FCSTD DOCUMENT  (FreeCAD 1.1R39215 (Git))
Label: folded_glasses_assembly
License: All rights reserved
LicenseURL: http://en.wikipedia.org/wiki/All_rights_reserved
objects: App::FeaturePython×7, App::Link×4, Assembly::JointGroup×1, Assembly::AssemblyObject×1
EXTERNAL_REF file=frame.FCStd obj=Body
EXTERNAL_REF file=lens_example.FCStd obj=Body
EXTERNAL_REF file=right_temple.FCStd obj=Part
EXTERNAL_REF file=left_temple.FCStd obj=Part__Mirroring

FEATURE [App::Link] Body  label="Frame"
  LinkedObject = -> <external frame.FCStd>#Body
FEATURE [App::FeaturePython] GroundedJoint  # Assembly grounded joint (typed FeaturePython)
  ObjectToGround = -> Body
FEATURE [App::Link] Body001  label="Right lens"
  LinkPlacement = pos=(32.7,1,-2e-16) rot=(0,0,1;0rad)
  LinkedObject = -> <external lens_example.FCStd>#Body
  Placement = pos=(32.7,1,-2e-16) rot=(0,0,1;0rad)
FEATURE [App::FeaturePython] Joint  label="Right lens centering"  # Assembly joint (typed FeaturePython)
  Activated = true
  AngleMax = 0
  AngleMin = 0
  Detach1 = false
  Detach2 = false
  Distance = 0
  Distance2 = 0
  EnableAngleMax = false
  EnableAngleMin = false
  EnableLengthMax = false
  EnableLengthMin = false
  JointType = 1 (Revolute)
  LengthMax = 0
  LengthMin = 0
  Placement2 = pos=(32.7,0,0) rot=(0,0,1;0rad)
  Reference1 = -> Assembly [Body001.Sketch006.Edge1,Body001.Sketch006.Edge1]
  Reference2 = -> Assembly [Body.Sketch.Edge8,Body.Sketch.Edge8]
FEATURE [App::FeaturePython] Joint001  label="Right lens orientation"  # Assembly joint (typed FeaturePython)
  Activated = true
  AngleMax = 0
  AngleMin = 0
  Detach1 = false
  Detach2 = false
  Distance = 0
  Distance2 = 0
  EnableAngleMax = false
  EnableAngleMin = false
  EnableLengthMax = false
  EnableLengthMin = false
  JointType = 6 (Parallel)
  LengthMax = 0
  LengthMin = 0
  Placement1 = pos=(19.9369,-1.45799,-0.00317788) rot=(0.707107,0,-0.707107;3.14159rad)
  Placement2 = pos=(-56.2,-6e-16,-2.525) rot=(0.57735,-0.57735,0.57735;4.18879rad)
  Reference1 = -> Assembly [Body001.Face3,Body001.Face3]
  Reference2 = -> Assembly [Body.Face11,Body.Face11]
FEATURE [App::Link] Right_temple  label="Right temple"
  LinkPlacement = pos=(56.2,-2.5,1.187e-13) rot=(0.224951,0,0.97437;4.59055rad)
  LinkedObject = -> <external right_temple.FCStd>#Part
  Placement = pos=(56.2,-2.5,1.187e-13) rot=(0.224951,0,0.97437;4.59055rad)
FEATURE [App::FeaturePython] Joint002  label="Right temple centering"  # Assembly joint (typed FeaturePython)
  Activated = true
  AngleMax = 0
  AngleMin = 0
  Detach1 = false
  Detach2 = false
  Distance = 0
  Distance2 = 0
  EnableAngleMax = false
  EnableAngleMin = false
  EnableLengthMax = false
  EnableLengthMin = false
  JointType = 1 (Revolute)
  LengthMax = 0
  LengthMin = 0
  Placement1 = pos=(-0.562378,1.2e-15,-2.43593) rot=(-0.704823,0.704823,0.080304;3.30186rad)
  Placement2 = pos=(55.6376,-2.5,-2.43593) rot=(-0.704823,0.704823,0.080304;3.30186rad)
  Reference1 = -> Assembly [Right_temple.Body.Fillet.Edge111,Right_temple.Body.Fillet.Edge111]
  Reference2 = -> Assembly [Body.SubtractivePipe001.Edge191,Body.SubtractivePipe001.Edge191]
FEATURE [App::FeaturePython] Joint003  label="Right temple opening"  # Assembly joint (typed FeaturePython)
  Activated = true
  AngleMax = 0
  AngleMin = 0
  Detach1 = false
  Detach2 = false
  Distance = 5.59
  Distance2 = 0
  EnableAngleMax = false
  EnableAngleMin = false
  EnableLengthMax = false
  EnableLengthMin = false
  JointType = 5 (Distance)
  LengthMax = 0
  LengthMin = 0
  Placement1 = pos=(56.2,1,-5) rot=(0,0,1;0rad)
  Placement2 = pos=(0.1,3.5,-5) rot=(0,0,1;0rad)
  Reference1 = -> Assembly [Body.SubtractivePipe001.Vertex16,Body.SubtractivePipe001.Vertex16]
  Reference2 = -> Assembly [Right_temple.Body.Fillet.Vertex63,Right_temple.Body.Fillet.Vertex63]
FEATURE [App::Link] Left_temple  label="Left temple"
  LinkPlacement = pos=(-56.2,-2.5,6.1e-14) rot=(-0.224951,0,0.97437;1.77201rad)
  LinkedObject = -> <external left_temple.FCStd>#Part__Mirroring
  Placement = pos=(-56.2,-2.5,6.1e-14) rot=(-0.224951,0,0.97437;1.77201rad)
FEATURE [App::FeaturePython] Joint004  label="Left temple centering"  # Assembly joint (typed FeaturePython)
  Activated = true
  AngleMax = 0
  AngleMin = 0
  Detach1 = false
  Detach2 = false
  Distance = 0
  Distance2 = 0
  EnableAngleMax = false
  EnableAngleMin = false
  EnableLengthMax = false
  EnableLengthMin = false
  JointType = 1 (Revolute)
  LengthMax = 0
  LengthMin = 0
  Placement1 = pos=(0.562378,7.1e-15,-2.43593) rot=(0.112485,-0.112485,-0.987266;1.58361rad)
  Placement2 = pos=(-55.6376,-2.5,-2.43593) rot=(0.112485,-0.112485,-0.987266;1.58361rad)
  Reference1 = -> Assembly [Left_temple.Edge111,Left_temple.Edge111]
  Reference2 = -> Assembly [Body.SubtractivePipe001.Edge123,Body.SubtractivePipe001.Edge123]
FEATURE [App::FeaturePython] Joint005  label="Left temple opening"  # Assembly joint (typed FeaturePython)
  Activated = true
  AngleMax = 0
  AngleMin = 0
  Detach1 = false
  Detach2 = false
  Distance = 5.777
  Distance2 = 0
  EnableAngleMax = false
  EnableAngleMin = false
  EnableLengthMax = false
  EnableLengthMin = false
  JointType = 5 (Distance)
  LengthMax = 0
  LengthMin = 0
  Placement1 = pos=(-56.2,1,-5) rot=(0,0,1;0rad)
  Placement2 = pos=(-0.1,3.5,-5) rot=(0,0,1;0rad)
  Reference1 = -> Assembly [Body.SubtractivePipe001.Vertex11,Body.SubtractivePipe001.Vertex11]
  Reference2 = -> Assembly [Left_temple.Vertex63,Left_temple.Vertex63]
FEATURE [Assembly::JointGroup] Joints
  Group = -> [GroundedJoint,Joint,Joint001,Joint002,Joint003,Joint004,Joint005]
FEATURE [Assembly::AssemblyObject] Assembly
  Group = -> [Joints,Body,GroundedJoint,Body001,Joint,Joint001,Right_temple,Joint002,Joint003,Left_temple,Joint004,Joint005]
  Origin = -> Origin
  Type = Assembly

RESOLVED EXTERNAL PARTS (link-assembly join: the EXTERNAL_REF files above that resolve inside this repo's crawl, each included once):
---- part frame.FCStd = doc fcstd_d1c061e1a5e6 ----
FCSTD DOCUMENT  (FreeCAD 1.1R39673 (Git))
Label: frame
License: All rights reserved
LicenseURL: http://en.wikipedia.org/wiki/All_rights_reserved
objects: Sketcher::SketchObject×15, PartDesign::Plane×6, PartDesign::Pad×3, PartDesign::Pocket×3, PartDesign::SubtractivePipe×2, PartDesign::Fillet×1, PartDesign::Line×1, PartDesign::AdditiveLoft×1, PartDesign::Mirrored×1, PartDesign::Body×1, App::Point×1
note: 70 computed .brp shape members not serialized (recipe doc carries the construction recipe); baked Part::Feature solids carry a one-line shape summary decoded from their .brp

FEATURE [Sketcher::SketchObject] Sketch  label="Lenses holder master sketch"
  ArcFitTolerance = 1e-06
  AttachmentSupport = -> [XZ_Plane]
  ExternalTypes = [0]
  FullyConstrained = true
  MakeInternals = false
  MapMode = 5
  Placement = pos=(0,0,0) rot=(1,0,0;1.5708rad)
  sketch-geometry (24):
    g0: Ellipse CenterX=-32.7 CenterY=0 CenterZ=0 NormalX=0 NormalY=0 NormalZ=1 MajorRadius=20 MinorRadius=19 AngleXU=-2.2e-15
    g1: LineSegment [constr] StartX=-12.7 StartY=0 StartZ=0 EndX=-52.7 EndY=0 EndZ=0
    g2: LineSegment [constr] StartX=-32.7 StartY=19 StartZ=0 EndX=-32.7 EndY=-19 EndZ=0
    g3: GeomPoint [constr] X=-26.455 Y=-1.37e-14 Z=0
    g4: GeomPoint [constr] X=-38.945 Y=1.39e-14 Z=0
    g5: Ellipse CenterX=32.7 CenterY=0 CenterZ=0 NormalX=0 NormalY=0 NormalZ=1 MajorRadius=20 MinorRadius=19 AngleXU=0
    g6: LineSegment [constr] StartX=52.7 StartY=0 StartZ=0 EndX=12.7 EndY=0 EndZ=0
    g7: LineSegment [constr] StartX=32.7 StartY=19 StartZ=0 EndX=32.7 EndY=-19 EndZ=0
    g8: GeomPoint [constr] X=38.945 Y=0 Z=0
    g9: GeomPoint [constr] X=26.455 Y=0 Z=0
    g10: ArcOfEllipse CenterX=-32.7 CenterY=0 CenterZ=0 NormalX=0 NormalY=0 NormalZ=1 MajorRadius=22 MinorRadius=21 AngleXU=-4.6e-15 StartAngle=0.410218 EndAngle=6.59162
    g11: LineSegment [constr] StartX=-10.7 StartY=0 StartZ=0 EndX=-54.7 EndY=0 EndZ=0
    g12: LineSegment [constr] StartX=-32.7 StartY=21 StartZ=0 EndX=-32.7 EndY=-21 EndZ=0
    g13: GeomPoint [constr] X=-26.1426 Y=-3.02e-14 Z=0
    g14: GeomPoint [constr] X=-39.2574 Y=3e-14 Z=0
    g15: ArcOfEllipse CenterX=32.7 CenterY=0 CenterZ=0 NormalX=0 NormalY=0 NormalZ=1 MajorRadius=22 MinorRadius=21 AngleXU=0 StartAngle=2.83315 EndAngle=9.01456
    g16: LineSegment [constr] StartX=54.7 StartY=0 StartZ=0 EndX=10.7 EndY=0 EndZ=0
    g17: LineSegment [constr] StartX=32.7 StartY=21 StartZ=0 EndX=32.7 EndY=-21 EndZ=0
    g18: GeomPoint [constr] X=39.2574 Y=0 Z=0
    g19: GeomPoint [constr] X=26.1426 Y=-3e-16 Z=0
    g20: LineSegment StartX=-11.7382 StartY=6.375 StartZ=0 EndX=11.7382 EndY=6.375 EndZ=0
    g21: LineSegment StartX=-12.5253 StartY=8.375 StartZ=0 EndX=12.5253 EndY=8.375 EndZ=0
    g22: Circle CenterX=-32.7 CenterY=0 CenterZ=0 NormalX=0 NormalY=0 NormalZ=1 AngleXU=0 Radius=0.5
    g23: Circle CenterX=32.7 CenterY=0 CenterZ=0 NormalX=0 NormalY=0 NormalZ=1 AngleXU=0 Radius=0.5
  constraints (33):
    c: InternalAlignment(g1-g4 -> g0) x4
    c: PointOnObject(g0,g-1)
    c: Horizontal(g1)
    c: DistanceX(g1,g1) = 40
    c: DistanceY(g2,g2) = 38
    c: InternalAlignment(g6-g9 -> g5) x4
    c: Horizontal(g6)
    c: Equal(g1,g6)
    c: Equal(g7,g2)
    c: Symmetric(g5,g0,g-2)
    c: DistanceX(g0,g5) = 65.4
    c: InternalAlignment(g11-g14 -> g10) x4
    c: Coincident(g10,g0)
    c: Horizontal(g11)
    c: InternalAlignment(g16-g19 -> g15) x4
    c: Symmetric(g0,g15,g-2)
    c: Horizontal(g16)
    c: Equal(g16,g11)
    c: Equal(g17,g12)
    c: Horizontal(g10,g15)
    c: Horizontal(g15,g10)
    c: Coincident(g20,g10)
    c: Coincident(g20,g15)
    c: Coincident(g21,g10)
    c: Coincident(g21,g15)
    c: Distance(g20,g21) = 2
    c: Distance(g-1,g20) = 6.375
    c: Coincident(g22,g0)
    c: Diameter(g22) = 1
    c: Equal(g22,g23)
    c: Symmetric(g22,g23,g-2)
    c: DistanceY(g12,g12) = 42
    c: DistanceX(g11,g11) = 44
FEATURE [PartDesign::Pad] Pad  label="Lenses holder"
  Direction = (0,-1,2e-16)
  Length = 2
  Length2 = 10
  Midplane = true
  Placement = pos=(0,0,0) rot=(1,0,0;1.5708rad)
  Profile = -> Sketch
  ReferenceAxis = -> Sketch [N_Axis]
  Suppressed = false
  Type = 0
FEATURE [Sketcher::SketchObject] Sketch001  label="Nose bridge profile #1"
  ArcFitTolerance = 1e-06
  AttachmentSupport = -> [YZ_Plane]
  ExternalTypes = [0]
  FullyConstrained = true
  MakeInternals = false
  MapMode = 5
  Placement = pos=(0,0,0) rot=(0.57735,0.57735,0.57735;2.0944rad)
  sketch-geometry (1):
    g0: LineSegment StartX=-6 StartY=0 StartZ=0 EndX=0 EndY=5.5 EndZ=0
  constraints (4):
    c: PointOnObject(g0,g-1)
    c: Distance(g0,g-1) = 5.5
    c: PointOnObject(g0,g-2)
    c: DistanceX(g0,g-1) = 6
FEATURE [Sketcher::SketchObject] Sketch002  label="Nose bridge profile #2"
  ArcFitTolerance = 1e-06
  AttachmentSupport = -> [XY_Plane]
  ExternalGeometry = -> [Sketch001]
  ExternalTypes = [0]
  FullyConstrained = true
  MakeInternals = false
  MapMode = 5
  sketch-geometry (1):
    g0: LineSegment StartX=-9.25 StartY=-6 StartZ=0 EndX=9.25 EndY=-6 EndZ=0
  constraints (3):
    c: Symmetric(g0,g0,g-2)
    c: PointOnObject(g-3,g0)
    c: DistanceX(g0,g0) = 18.5
FEATURE [PartDesign::Plane] DatumPlane  label="Nose bridge plane"
  AttachmentSupport = -> [Sketch001,Sketch002]
  Length = 134.588
  MapMode = 13
  Placement = pos=(0,-4,1.83333) rot=(1,0,0;0.741947rad)
  ResizeMode = 0
  Width = 88.7838
FEATURE [Sketcher::SketchObject] Sketch003  label="Nose bridge profile"
  ArcFitTolerance = 1e-06
  AttachmentSupport = -> [DatumPlane]
  ExternalGeometry = -> [Sketch001,Sketch002,Pad]
  ExternalTypes = [0]
  FullyConstrained = true
  MakeInternals = false
  MapMode = 5
  Placement = pos=(0,-4,1.83333) rot=(1,0,0;0.741947rad)
  sketch-geometry (21):
    g0: ArcOfEllipse CenterX=0 CenterY=-15.7131 CenterZ=0 NormalX=0 NormalY=0 NormalZ=1 MajorRadius=21.1394 MinorRadius=11.7303 AngleXU=1.5708 StartAngle=5.37473 EndAngle=7.19164
    g1: LineSegment [constr] StartX=0 StartY=5.42627 StartZ=0 EndX=0 EndY=-36.8525 EndZ=0
    g2: LineSegment [constr] StartX=-11.7303 StartY=-15.7131 StartZ=0 EndX=11.7303 EndY=-15.7131 EndZ=0
    g3: GeomPoint [constr] X=2e-15 Y=1.87305 Z=0
    g4: GeomPoint [constr] X=0 Y=-33.2993 Z=0
    g5: ArcOfEllipse CenterX=0 CenterY=-15.7131 CenterZ=0 NormalX=0 NormalY=0 NormalZ=1 MajorRadius=22.4394 MinorRadius=13.7303 AngleXU=1.5708 StartAngle=5.71213 EndAngle=6.85424
    g6: LineSegment [constr] StartX=-5e-16 StartY=6.72627 StartZ=0 EndX=5e-16 EndY=-38.1525 EndZ=0
    g7: LineSegment [constr] StartX=-13.7303 StartY=-15.7131 StartZ=0 EndX=13.7303 EndY=-15.7131 EndZ=0
    g8: GeomPoint [constr] X=2e-15 Y=2.03525 Z=0
    g9: GeomPoint [constr] X=4e-16 Y=-33.4615 Z=0
    g10: ArcOfCircle CenterX=-10.3972 CenterY=-2.21669 CenterZ=0 NormalX=0 NormalY=0 NormalZ=1 AngleXU=0 Radius=1.25 StartAngle=3.37719 EndAngle=5.87477
    g11: LineSegment StartX=-13.82 StartY=6.68686 StartZ=0 EndX=-11.6127 EndY=-2.50847 EndZ=0
    g12: GeomPoint [constr] X=-9.25 Y=-2.71314 Z=0
    g13: LineSegment StartX=11.6127 StartY=-2.50847 StartZ=0 EndX=13.82 EndY=6.68686 EndZ=0
    g14: ArcOfCircle CenterX=10.3972 CenterY=-2.21669 CenterZ=0 NormalX=0 NormalY=0 NormalZ=1 AngleXU=0 Radius=1.25 StartAngle=3.55001 EndAngle=6.04759
    g15: ArcOfCircle CenterX=-9.05082 CenterY=4.71757 CenterZ=0 NormalX=0 NormalY=0 NormalZ=1 AngleXU=0 Radius=2.25 StartAngle=3.63126 EndAngle=5.52216
    g16: LineSegment StartX=-11.0364 StartY=3.65931 StartZ=0 EndX=-12.65 EndY=6.68686 EndZ=0
    g17: ArcOfCircle CenterX=9.05082 CenterY=4.71757 CenterZ=0 NormalX=0 NormalY=0 NormalZ=1 AngleXU=0 Radius=2.25 StartAngle=3.90262 EndAngle=5.79351
    g18: LineSegment StartX=11.0364 StartY=3.65931 StartZ=0 EndX=12.65 EndY=6.68686 EndZ=0
    g19: LineSegment StartX=-13.82 StartY=6.68686 StartZ=0 EndX=-12.65 EndY=6.68686 EndZ=0
    g20: LineSegment StartX=12.65 StartY=6.68686 StartZ=0 EndX=13.82 EndY=6.68686 EndZ=0
  constraints (39):
    c: InternalAlignment(g1-g4 -> g0) x4
    c: PointOnObject(g0,g-2)
    c: Coincident(g-3,g1)
    c: PointOnObject(g-4,g0)
    c: Distance(g0,g-4) = 13
    c: InternalAlignment(g6-g9 -> g5) x4
    c: Coincident(g5,g0)
    c: DistanceY(g1,g6) = 1.3
    c: Distance(g2,g7) = 2
    c: Horizontal(g7)
    c: Tangent(g10,g11) = -1.5708
    c: Coincident(g-4,g10)
    c: PointOnObject(g12,g0)
    c: PointOnObject(g12,g10)
    c: Tangent(g0,g10,g12) = 1.5708
    c: Symmetric(g10,g13,g-2)
    c: Coincident(g-4,g14)
    c: Tangent(g13,g14) = -1.5708
    c: PointOnObject(g0,g-4)
    c: PointOnObject(g0,g-4)
    c: Radius(g10) = 1.25
    c: Horizontal(g5,g5)
    c: Coincident(g15,g5)
    c: Tangent(g16,g15) = 1.5708
    c: Symmetric(g15,g17,g-2)
    c: Tangent(g17,g5) = 1.5708
    c: Tangent(g18,g17) = -1.5708
    c: Radius(g15) = 2.25
    c: Distance(g15,g11) = 2
    c: Horizontal(g19)
    c: Distance(g19,g-4) = 9.4
    c: DistanceX(g19,g-1) = 13.82
    c: Distance(g19,g-2) = 12.65
    c: Coincident(g11,g19)
    c: Coincident(g16,g19)
    c: Symmetric(g11,g13,g-2)
    c: Symmetric(g16,g18,g-2)
    c: Coincident(g20,g18)
    c: Coincident(g20,g13)
FEATURE [PartDesign::Pad] Pad001  label="Nose bridge #1"
  BaseFeature = -> Pad
  Direction = (0,-0.675725,0.737154)
  Length = 2.8
  Length2 = 10
  Placement = pos=(0,0,0) rot=(1,0,0;1.5708rad)
  Profile = -> Sketch003
  ReferenceAxis = -> Sketch003 [N_Axis]
  Refine = true
  Suppressed = false
  Type = 0
FEATURE [Sketcher::SketchObject] Sketch010
  ArcFitTolerance = 1e-06
  AttachmentSupport = -> [Pad001]
  ExternalGeometry = -> [Pad001]
  ExternalTypes = [0]
  FullyConstrained = true
  MakeInternals = false
  MapMode = 5
  Placement = pos=(0,1.9e-15,8.375) rot=(0,0,1;3.14159rad)
  sketch-geometry (4):
    g0: LineSegment StartX=-12.5253 StartY=1 StartZ=0 EndX=-12.5253 EndY=-1 EndZ=0
    g1: LineSegment StartX=-12.5253 StartY=-1 StartZ=0 EndX=12.5253 EndY=-1 EndZ=0
    g2: LineSegment StartX=12.5253 StartY=-1 StartZ=0 EndX=12.5253 EndY=1 EndZ=0
    g3: LineSegment StartX=12.5253 StartY=1 StartZ=0 EndX=-12.5253 EndY=1 EndZ=0
  constraints (10):
    c: Coincident(g0,g1)
    c: Coincident(g1,g2)
    c: Coincident(g2,g3)
    c: Coincident(g3,g0)
    c: Vertical(g0)
    c: Vertical(g2)
    c: Horizontal(g1)
    c: Horizontal(g3)
    c: Coincident(g-3,g0)
    c: Coincident(g-4,g1)
FEATURE [PartDesign::Pocket] Pocket002  label="Nose bridge #2"
  BaseFeature = -> Pad001
  Direction = (0,0,-1)
  Length = 5
  Length2 = 5
  Placement = pos=(0,0,0) rot=(1,0,0;1.5708rad)
  Profile = -> Sketch010
  ReferenceAxis = -> Sketch010 [N_Axis]
  Refine = true
  Reversed = true
  Suppressed = false
  Type = 1
FEATURE [Sketcher::SketchObject] Sketch011
  ArcFitTolerance = 1e-06
  AttachmentSupport = -> [DatumPlane]
  ExternalGeometry = -> [Pocket002]
  ExternalTypes = [0]
  FullyConstrained = true
  MakeInternals = false
  MapMode = 5
  Placement = pos=(0,-4,1.83333) rot=(1,0,0;0.741947rad)
  sketch-geometry (5):
    g0: Ellipse CenterX=0 CenterY=-15.7131 CenterZ=0 NormalX=0 NormalY=0 NormalZ=1 MajorRadius=21.1394 MinorRadius=11.7303 AngleXU=1.5708
    g1: LineSegment [constr] StartX=0 StartY=5.42627 StartZ=0 EndX=0 EndY=-36.8525 EndZ=0
    g2: LineSegment [constr] StartX=-11.7303 StartY=-15.7131 StartZ=0 EndX=11.7303 EndY=-15.7131 EndZ=0
    g3: GeomPoint [constr] X=2e-15 Y=1.87305 Z=0
    g4: GeomPoint [constr] X=4e-16 Y=-33.2993 Z=0
  constraints (4):
    c: InternalAlignment(g1-g4 -> g0) x4
    c: Coincident(g0,g-3)
    c: Equal(g-3,g0)
    c: Vertical(g1)
FEATURE [PartDesign::Pocket] Pocket003  label="Nose bridge #3"
  BaseFeature = -> Pocket002
  Direction = (0,0.675725,-0.737154)
  Length = 5
  Length2 = 5
  Midplane = true
  Placement = pos=(0,0,0) rot=(1,0,0;1.5708rad)
  Profile = -> Sketch011
  ReferenceAxis = -> Sketch011 [N_Axis]
  Refine = true
  Suppressed = false
  Type = 1
FEATURE [PartDesign::Fillet] Fillet  label="Nose bridge #4"
  Base = -> Pocket003 [Edge55,Edge54,Edge40]
  BaseFeature = -> Pocket003
  Placement = pos=(0,0,0) rot=(1,0,0;1.5708rad)
  Radius = 0.6
  Refine = true
  SupportTransform = false
  Suppressed = false
  UseAllEdges = false
FEATURE [Sketcher::SketchObject] Sketch008  label="Hinges mid profile"
  ArcFitTolerance = 1e-06
  AttachmentSupport = -> [XY_Plane]
  ExternalGeometry = -> [Fillet]
  ExternalTypes = [0]
  FullyConstrained = true
  MakeInternals = false
  MapMode = 5
  sketch-geometry (14):
    g0: Circle CenterX=-56.2 CenterY=-2.5 CenterZ=0 NormalX=0 NormalY=0 NormalZ=1 AngleXU=0 Radius=0.55
    g1: Circle [constr] CenterX=-56.2 CenterY=-2.5 CenterZ=0 NormalX=0 NormalY=0 NormalZ=1 AngleXU=0 Radius=1.5
    g2: LineSegment [constr] StartX=-54.7 StartY=1 StartZ=0 EndX=-54.7 EndY=-1 EndZ=0
    g3: ArcOfCircle CenterX=-56.2 CenterY=-2.5 CenterZ=0 NormalX=0 NormalY=0 NormalZ=1 AngleXU=0 Radius=1.5 StartAngle=1.5708 EndAngle=6.28319
    g4: ArcOfCircle CenterX=-53.2 CenterY=-2.5 CenterZ=0 NormalX=0 NormalY=0 NormalZ=1 AngleXU=0 Radius=1.5 StartAngle=1.5708 EndAngle=3.14159
    g5: LineSegment StartX=-53.2 StartY=-1 StartZ=0 EndX=-53.2 EndY=1 EndZ=0
    g6: LineSegment StartX=-56.2 StartY=1 StartZ=0 EndX=-53.2 EndY=1 EndZ=0
    g7: Circle CenterX=56.2 CenterY=-2.5 CenterZ=0 NormalX=0 NormalY=0 NormalZ=1 AngleXU=0 Radius=0.55
    g8: ArcOfCircle CenterX=56.2 CenterY=-2.5 CenterZ=0 NormalX=0 NormalY=0 NormalZ=1 AngleXU=0 Radius=1.5 StartAngle=3.14159 EndAngle=7.85398
    g9: ArcOfCircle CenterX=53.2 CenterY=-2.5 CenterZ=0 NormalX=0 NormalY=0 NormalZ=1 AngleXU=0 Radius=1.5 StartAngle=0 EndAngle=1.5708
    g10: LineSegment StartX=53.2 StartY=-1 StartZ=0 EndX=53.2 EndY=1 EndZ=0
    g11: LineSegment StartX=56.2 StartY=1 StartZ=0 EndX=53.2 EndY=1 EndZ=0
    g12: LineSegment StartX=-56.2 StartY=-1 StartZ=0 EndX=-56.2 EndY=1 EndZ=0
    g13: LineSegment StartX=56.2 StartY=-1 StartZ=0 EndX=56.2 EndY=1 EndZ=0
  constraints (39):
    c: Coincident(g1,g0)
    c: Diameter(g1) = 3
    c: Diameter(g0) = 1.1
    c: Tangent(g1,g2)
    c: Coincident(g3,g0)
    c: Equal(g1,g3)
    c: Horizontal(g3,g0)
    c: Coincident(g4,g3)
    c: Horizontal(g4,g0)
    c: Vertical(g4,g4)
    c: Vertical(g5)
    c: Coincident(g6,g5)
    c: Horizontal(g6)
    c: PointOnObject(g2,g6)
    c: Coincident(g8,g7)
    c: Coincident(g9,g8)
    c: Coincident(g11,g10)
    c: Symmetric(g0,g7,g-2)
    c: Symmetric(g9,g4,g-2)
    c: Symmetric(g10,g5,g-2)
    c: Horizontal(g11)
    c: Equal(g8,g3)
    c: Horizontal(g9,g8)
    c: Vertical(g9,g9)
    c: Equal(g7,g0)
    c: Vertical(g0,g3)
    c: Coincident(g12,g3)
    c: Coincident(g12,g6)
    c: Vertical(g7,g8)
    c: Coincident(g13,g8)
    c: Coincident(g13,g11)
    c: Vertical(g13)
    c: Horizontal(g5,g2)
    c: Coincident(g5,g4)
    c: Coincident(g10,g9)
    c: Coincident(g2,g-3)
    c: Vertical(g2)
    c: Tangent(g1,g-3)
    c: Symmetric(g6,g3,g-1)
FEATURE [Sketcher::SketchObject] Sketch012
  ArcFitTolerance = 1e-06
  AttachmentSupport = -> [XY_Plane]
  ExternalGeometry = -> [Sketch008]
  ExternalTypes = [0]
  FullyConstrained = true
  MakeInternals = false
  MapMode = 5
  sketch-geometry (8):
    g0: LineSegment StartX=-53.2 StartY=1 StartZ=0 EndX=-56.2 EndY=1 EndZ=0
    g1: LineSegment StartX=-56.2 StartY=1 StartZ=0 EndX=-56.2 EndY=-1 EndZ=0
    g2: LineSegment StartX=-56.2 StartY=-1 StartZ=0 EndX=-53.2 EndY=-1 EndZ=0
    g3: LineSegment StartX=-53.2 StartY=-1 StartZ=0 EndX=-53.2 EndY=1 EndZ=0
    g4: LineSegment StartX=53.2 StartY=-1 StartZ=0 EndX=53.2 EndY=1 EndZ=0
    g5: LineSegment StartX=53.2 StartY=1 StartZ=0 EndX=56.2 EndY=1 EndZ=0
    g6: LineSegment StartX=56.2 StartY=1 StartZ=0 EndX=56.2 EndY=-1 EndZ=0
    g7: LineSegment StartX=56.2 StartY=-1 StartZ=0 EndX=53.2 EndY=-1 EndZ=0
  constraints (20):
    c: Coincident(g0,g1)
    c: Coincident(g1,g2)
    c: Coincident(g2,g3)
    c: Coincident(g3,g0)
    c: Horizontal(g0)
    c: Horizontal(g2)
    c: Vertical(g1)
    c: Vertical(g3)
    c: Coincident(g0,g-3)
    c: Coincident(g1,g-4)
    c: Coincident(g4,g5)
    c: Coincident(g5,g6)
    c: Coincident(g6,g7)
    c: Coincident(g7,g4)
    c: Symmetric(g6,g1,g-2)
    c: Symmetric(g4,g0,g-2)
    c: Horizontal(g5)
    c: Vertical(g6)
    c: Vertical(g4)
    c: Horizontal(g7)
FEATURE [Sketcher::SketchObject] Sketch014  label="Lens grooves paths"
  ArcFitTolerance = 1e-06
  AttachmentSupport = -> [XZ_Plane]
  ExternalGeometry = -> [Sketch]
  ExternalTypes = [0]
  FullyConstrained = true
  MakeInternals = false
  MapMode = 5
  Placement = pos=(0,0,0) rot=(1,0,0;1.5708rad)
  sketch-geometry (13):
    g0: ArcOfEllipse CenterX=32.7 CenterY=0 CenterZ=0 NormalX=0 NormalY=0 NormalZ=1 MajorRadius=20 MinorRadius=19 AngleXU=1e-16 StartAngle=0.0770976 EndAngle=6.20609
    g1: LineSegment [constr] StartX=52.7 StartY=1.2e-15 StartZ=0 EndX=12.7 EndY=-1.2e-15 EndZ=0
    g2: LineSegment [constr] StartX=32.7 StartY=19 StartZ=0 EndX=32.7 EndY=-19 EndZ=0
    g3: GeomPoint [constr] X=38.945 Y=6e-16 Z=0
    g4: GeomPoint [constr] X=26.455 Y=-4e-16 Z=0
    g5: LineSegment [constr] StartX=52.6406 StartY=1.4634 StartZ=0 EndX=52.6406 EndY=-1.4634 EndZ=0
    g6: LineSegment [constr] StartX=32.7 StartY=0 StartZ=0 EndX=53.1392 EndY=1.5 EndZ=0
    g7: LineSegment [constr] StartX=32.7 StartY=0 StartZ=0 EndX=53.1392 EndY=-1.5 EndZ=0
    g8: ArcOfEllipse CenterX=-32.7 CenterY=3.35e-14 CenterZ=0 NormalX=0 NormalY=0 NormalZ=1 MajorRadius=20 MinorRadius=19 AngleXU=-3.14159 StartAngle=0.0770976 EndAngle=6.20609
    g9: LineSegment [constr] StartX=-52.7 StartY=3.19e-14 StartZ=0 EndX=-12.7 EndY=3.51e-14 EndZ=0
    g10: LineSegment [constr] StartX=-32.7 StartY=19 StartZ=0 EndX=-32.7 EndY=-19 EndZ=0
    g11: GeomPoint [constr] X=-38.945 Y=3.27e-14 Z=0
    g12: GeomPoint [constr] X=-26.455 Y=3.4e-14 Z=0
  constraints (20):
    c: InternalAlignment(g1-g4 -> g0) x4
    c: Coincident(g0,g-3)
    c: Equal(g0,g-3)
    c: Vertical(g2)
    c: Vertical(g5)
    c: Coincident(g0,g5)
    c: Coincident(g0,g5)
    c: Coincident(g6,g0)
    c: Coincident(g7,g0)
    c: PointOnObject(g0,g6)
    c: PointOnObject(g0,g7)
    c: Equal(g6,g7)
    c: Distance(g0,g6) = 0.5
    c: DistanceY(g7,g6) = 3
    c: InternalAlignment(g9-g12 -> g8) x4
    c: Vertical(g10)
    c: Symmetric(g8,g0,g-2)
    c: Symmetric(g8,g0,g-2)
    c: Equal(g9,g1)
    c: Equal(g10,g2)
FEATURE [PartDesign::Plane] DatumPlane001  label="Right lens groove start plane"
  AttachmentSupport = -> [Sketch014]
  Length = 92.1419
  MapMode = 8
  Placement = pos=(52.6406,3e-16,1.4634) rot=(0.999177,0,0.040558;3.14159rad)
  ResizeMode = 0
  Width = 62.6119
FEATURE [PartDesign::Plane] DatumPlane002  label="Left lens groove start plane"
  AttachmentSupport = -> [Sketch014]
  Length = 92.1419
  MapMode = 8
  Placement = pos=(-52.6406,3e-16,1.4634) rot=(0.040558,0,0.999177;3.14159rad)
  ResizeMode = 0
  Width = 62.6119
FEATURE [PartDesign::Plane] DatumPlane003  label="Through-hinges vertical plane"
  AttachmentSupport = -> [XZ_Plane,Sketch008]
  Length = 60
  MapMode = 53
  Placement = pos=(0,-2.5,-6e-16) rot=(1,0,0;1.5708rad)
  ResizeMode = 0
  Width = 60
FEATURE [Sketcher::SketchObject] Sketch017  label="Hinges axes"
  ArcFitTolerance = 1e-06
  AttachmentSupport = -> [DatumPlane003]
  ExternalGeometry = -> [Sketch008]
  ExternalTypes = [0]
  FullyConstrained = true
  MakeInternals = false
  MapMode = 5
  Placement = pos=(0,-2.5,-6e-16) rot=(1,0,0;1.5708rad)
  sketch-geometry (5):
    g0: LineSegment [constr] StartX=-56.75 StartY=6e-16 StartZ=0 EndX=-56.2 EndY=6e-16 EndZ=0
    g1: LineSegment [constr] StartX=-55.65 StartY=6e-16 StartZ=0 EndX=-56.2 EndY=6e-16 EndZ=0
    g2: LineSegment StartX=-56.7624 StartY=2.43593 StartZ=0 EndX=-55.6376 EndY=-2.43593 EndZ=0
    g3: LineSegment [constr] StartX=-56.2 StartY=6e-16 StartZ=0 EndX=-56.2 EndY=2.43593 EndZ=0
    g4: LineSegment StartX=56.7624 StartY=2.43593 StartZ=0 EndX=55.6376 EndY=-2.43593 EndZ=0
  constraints (12):
    c: Coincident(g0,g-3)
    c: Coincident(g1,g-3)
    c: Coincident(g1,g0)
    c: Symmetric(g1,g0,g0)
    c: Coincident(g3,g0)
    c: Vertical(g3)
    c: Symmetric(g2,g2,g0)
    c: Horizontal(g3,g2)
    c: Angle(g3,g2) = 0.226893
    c: Distance(g2,g2) = 5
    c: Symmetric(g2,g4,g-2)
    c: Symmetric(g2,g4,g-2)
FEATURE [PartDesign::Pad] Pad003  label="End pieces"
  BaseFeature = -> Fillet
  Direction = (0,0,1)
  Length = 10
  Length2 = 10
  Midplane = true
  Placement = pos=(0,0,0) rot=(1,0,0;1.5708rad)
  Profile = -> Sketch012
  ReferenceAxis = -> Sketch012 [N_Axis]
  Refine = true
  Suppressed = false
  Type = 0
FEATURE [PartDesign::Plane] DatumPlane004  label="Left hinge top profile plane"
  AttachmentSupport = -> [Sketch017]
  Length = 63.0187
  MapMode = 7
  Placement = pos=(-56.7624,-2.5,2.43593) rot=(0.112485,-0.112485,-0.987266;1.58361rad)
  ResizeMode = 0
  Width = 97.7613
FEATURE [PartDesign::Plane] DatumPlane005  label="Left hinge bottom profile plane"
  AttachmentSupport = -> [Sketch017]
  Length = 63.0187
  MapMode = 7
  Placement = pos=(-55.6376,-2.5,-2.43593) rot=(0.112485,-0.112485,-0.987266;1.58361rad)
  ResizeMode = 0
  Width = 97.7613
FEATURE [Sketcher::SketchObject] Sketch018
  ArcFitTolerance = 1e-06
  AttachmentSupport = -> [DatumPlane004]
  ExternalGeometry = -> [Sketch008]
  ExternalTypes = [0]
  FullyConstrained = true
  MakeInternals = false
  MapMode = 5
  Placement = pos=(-56.7624,-2.5,2.43593) rot=(0.112485,-0.112485,-0.987266;1.58361rad)
  sketch-geometry (7):
    g0: LineSegment [constr] StartX=0 StartY=0 StartZ=0 EndX=0.55 EndY=0 EndZ=0
    g1: LineSegment [constr] StartX=0.55 StartY=0 StartZ=0 EndX=1.5 EndY=0 EndZ=0
    g2: Circle CenterX=0 CenterY=0 CenterZ=0 NormalX=0 NormalY=0 NormalZ=1 AngleXU=0 Radius=0.55
    g3: ArcOfCircle CenterX=0 CenterY=0 CenterZ=0 NormalX=0 NormalY=0 NormalZ=1 AngleXU=0 Radius=1.5 StartAngle=3.87634 EndAngle=7.85398
    g4: LineSegment StartX=-1.5 StartY=0 StartZ=0 EndX=-1.5 EndY=2.92311 EndZ=0
    g5: ArcOfEllipse CenterX=-2e-16 CenterY=2.92311 CenterZ=0 NormalX=0 NormalY=0 NormalZ=1 MajorRadius=1.5 MinorRadius=1.42311 AngleXU=-3.14159 StartAngle=0 EndAngle=1.5708
    g6: ArcOfCircle CenterX=0 CenterY=0 CenterZ=0 NormalX=0 NormalY=0 NormalZ=1 AngleXU=0 Radius=1.5 StartAngle=3.14159 EndAngle=3.87634
  constraints (21):
    c: Coincident(g0,g-1)
    c: PointOnObject(g0,g-4)
    c: Coincident(g1,g0)
    c: PointOnObject(g1,g-3)
    c: Horizontal(g0)
    c: Horizontal(g1)
    c: Coincident(g2,g0)
    c: PointOnObject(g0,g2)
    c: Coincident(g3,g0)
    c: PointOnObject(g4,g-1)
    c: PointOnObject(g1,g3)
    c: PointOnObject(g3,g-2)
    c: Coincident(g4,g-5)
    c: Horizontal(g4,g5)
    c: Tangent(g5,g3) = 1.5708
    c: Tangent(g5,g4) = 1.5708
    c: Distance(g3,g4) = 0.387
    c: PointOnObject(g4,g-3)
    c: Coincident(g6,g0)
    c: Coincident(g3,g6)
    c: PointOnObject(g6,g-1)
FEATURE [Sketcher::SketchObject] Sketch013
  ArcFitTolerance = 1e-06
  AttachmentSupport = -> [XZ_Plane]
  ExternalGeometry = -> [Sketch,Sketch018]
  ExternalTypes = [0]
  FullyConstrained = true
  MakeInternals = false
  MapMode = 5
  Placement = pos=(0,0,0) rot=(1,0,0;1.5708rad)
  sketch-geometry (8):
    g0: LineSegment StartX=-58.2239 StartY=-0.05 StartZ=0 EndX=-58.2239 EndY=0.05 EndZ=0
    g1: LineSegment StartX=-58.2239 StartY=0.05 StartZ=0 EndX=-52.6999 EndY=0.05 EndZ=0
    g2: LineSegment StartX=-52.6999 StartY=0.05 StartZ=0 EndX=-52.6999 EndY=-0.05 EndZ=0
    g3: LineSegment StartX=-52.6999 StartY=-0.05 StartZ=0 EndX=-58.2239 EndY=-0.05 EndZ=0
    g4: LineSegment StartX=52.6999 StartY=-0.05 StartZ=0 EndX=52.6999 EndY=0.05 EndZ=0
    g5: LineSegment StartX=52.6999 StartY=0.05 StartZ=0 EndX=58.2239 EndY=0.05 EndZ=0
    g6: LineSegment StartX=58.2239 StartY=0.05 StartZ=0 EndX=58.2239 EndY=-0.05 EndZ=0
    g7: LineSegment StartX=58.2239 StartY=-0.05 StartZ=0 EndX=52.6999 EndY=-0.05 EndZ=0
  constraints (20):
    c: Coincident(g0,g1)
    c: Coincident(g2,g3)
    c: Coincident(g3,g0)
    c: Symmetric(g0,g0,g-1)
    c: Symmetric(g2,g1,g-1)
    c: Coincident(g1,g2)
    c: Horizontal(g1)
    c: Coincident(g4,g5)
    c: Coincident(g5,g6)
    c: Coincident(g6,g7)
    c: Coincident(g7,g4)
    c: Symmetric(g0,g5,g-2)
    c: Symmetric(g2,g4,g-2)
    c: Vertical(g4)
    c: Vertical(g6)
    c: Horizontal(g7)
    c: Horizontal(g5)
    c: DistanceY(g0,g0) = 0.1
    c: PointOnObject(g1,g-3)
    c: PointOnObject(g-4,g0)
FEATURE [PartDesign::Line] DatumLine001  label="Edge of left endpiece on left hinge bottom profile plane"
  AttacherType = Attacher::AttachEngineLine
  AttachmentSupport = -> [DatumPlane005,Pad003]
  Length = 20
  MapMode = 30
  Placement = pos=(-56.2,-2.5,-2.56576) rot=(0,0.707107,0.707107;3.14159rad)
  ResizeMode = 0
FEATURE [Sketcher::SketchObject] Sketch019
  ArcFitTolerance = 1e-06
  AttachmentSupport = -> [DatumPlane005]
  ExternalGeometry = -> [Sketch008,DatumLine001]
  ExternalTypes = [0]
  FullyConstrained = true
  MakeInternals = false
  MapMode = 5
  Placement = pos=(-55.6376,-2.5,-2.43593) rot=(0.112485,-0.112485,-0.987266;1.58361rad)
  sketch-geometry (7):
    g0: LineSegment [constr] StartX=0 StartY=0 StartZ=0 EndX=0.55 EndY=0 EndZ=0
    g1: LineSegment [constr] StartX=0.55 StartY=0 StartZ=0 EndX=1.5 EndY=0 EndZ=0
    g2: Circle CenterX=0 CenterY=0 CenterZ=0 NormalX=0 NormalY=0 NormalZ=1 AngleXU=0 Radius=0.55
    g3: ArcOfCircle CenterX=0 CenterY=0 CenterZ=0 NormalX=0 NormalY=0 NormalZ=1 AngleXU=0 Radius=1.5 StartAngle=3.87623 EndAngle=7.85398
    g4: LineSegment StartX=-1.11311 StartY=-1.00547 StartZ=0 EndX=-1.5 EndY=-0.57717 EndZ=0
    g5: LineSegment StartX=-1.5 StartY=-0.57717 StartZ=0 EndX=-1.5 EndY=2.92311 EndZ=0
    g6: ArcOfEllipse CenterX=0 CenterY=2.92311 CenterZ=0 NormalX=0 NormalY=0 NormalZ=1 MajorRadius=1.5 MinorRadius=1.42311 AngleXU=9e-16 StartAngle=3.14159 EndAngle=4.71239
  constraints (20):
    c: Coincident(g0,g-4)
    c: PointOnObject(g0,g-3)
    c: Coincident(g0,g1)
    c: PointOnObject(g1,g-4)
    c: Horizontal(g0)
    c: Horizontal(g1)
    c: Coincident(g2,g0)
    c: PointOnObject(g0,g2)
    c: Coincident(g3,g0)
    c: PointOnObject(g3,g-2)
    c: PointOnObject(g1,g3)
    c: PointOnObject(g4,g-5)
    c: Coincident(g5,g4)
    c: Vertical(g5)
    c: Tangent(g4,g3) = 1.5708
    c: Tangent(g5,g6) = 1.5708
    c: Coincident(g5,g-6)
    c: Tangent(g6,g3) = 1.5708
    c: PointOnObject(g6,g-2)
    c: Distance(g3,g5) = 0.386887
FEATURE [PartDesign::AdditiveLoft] AdditiveLoft  label="Left hinge"
  BaseFeature = -> Pad003
  Closed = false
  Placement = pos=(0,0,0) rot=(1,0,0;1.5708rad)
  Profile = -> Sketch018
  Refine = true
  Ruled = false
  Sections = -> [Sketch019]
  Suppressed = false
FEATURE [PartDesign::Mirrored] Mirrored  label="Right hinge"
  BaseFeature = -> AdditiveLoft
  MirrorPlane = -> YZ_Plane
  Originals = -> [AdditiveLoft]
  Placement = pos=(0,0,0) rot=(1,0,0;1.5708rad)
  Suppressed = false
  TransformMode = 0
FEATURE [PartDesign::Pocket] Pocket  label="Frame opening slits"
  BaseFeature = -> Mirrored
  Direction = (0,1,-2e-16)
  Length = 5
  Length2 = 5
  Midplane = true
  Placement = pos=(0,0,0) rot=(1,0,0;1.5708rad)
  Profile = -> Sketch013
  ReferenceAxis = -> Sketch013 [N_Axis]
  Refine = true
  Suppressed = false
  Type = 1
FEATURE [Sketcher::SketchObject] Sketch015  label="Right lens groove profile"
  ArcFitTolerance = 1e-06
  AttachmentSupport = -> [DatumPlane001]
  ExternalGeometry = -> [Pocket]
  ExternalTypes = [0]
  FullyConstrained = true
  MakeInternals = false
  MapMode = 5
  Placement = pos=(52.6406,3e-16,1.4634) rot=(0.999177,0,0.040558;3.14159rad)
  sketch-geometry (6):
    g0: LineSegment StartX=0 StartY=0.85 StartZ=0 EndX=0.490748 EndY=0 EndZ=0
    g1: LineSegment StartX=0 StartY=-0.85 StartZ=0 EndX=0.490748 EndY=0 EndZ=0
    g2: LineSegment [constr] StartX=0 StartY=-0.85 StartZ=0 EndX=0 EndY=0.85 EndZ=0
    g3: LineSegment StartX=0 StartY=0.85 StartZ=0 EndX=-0.490748 EndY=1.7 EndZ=0
    g4: LineSegment StartX=-0.490748 StartY=1.7 StartZ=0 EndX=-0.490748 EndY=-1.7 EndZ=0
    g5: LineSegment StartX=-0.490748 StartY=-1.7 StartZ=0 EndX=0 EndY=-0.85 EndZ=0
  constraints (17):
    c: PointOnObject(g0,g-2)
    c: PointOnObject(g0,g-1)
    c: PointOnObject(g1,g-2)
    c: Coincident(g1,g0)
    c: Coincident(g2,g1)
    c: Coincident(g2,g0)
    c: Angle(g0,g1) = 2.0944
    c: Equal(g1,g0)
    c: Coincident(g0,g3)
    c: Coincident(g3,g4)
    c: Vertical(g4)
    c: Coincident(g4,g5)
    c: Coincident(g5,g1)
    c: Parallel(g5,g1)
    c: Equal(g5,g1)
    c: Parallel(g3,g0)
    c: Distance(g1,g-4) = 0.15
FEATURE [PartDesign::SubtractivePipe] SubtractivePipe  label="Right lens groove"
  AuxilleryCurvelinear = true
  AuxillerySpineTangent = false
  BaseFeature = -> Pocket
  Binormal = (0,0,0)
  Mode = 0
  Placement = pos=(0,0,0) rot=(1,0,0;1.5708rad)
  Profile = -> Sketch015
  Refine = true
  Spine = -> Sketch014 [Edge1]
  SpineTangent = false
  Suppressed = false
  Transformation = 0
  Transition = 0
FEATURE [Sketcher::SketchObject] Sketch016  label="Left lens groove profile"
  ArcFitTolerance = 1e-06
  AttachmentSupport = -> [DatumPlane002]
  ExternalGeometry = -> [SubtractivePipe,Sketch015]
  ExternalTypes = [0]
  FullyConstrained = true
  MakeInternals = false
  MapMode = 5
  Placement = pos=(-52.6406,3e-16,1.4634) rot=(0.040558,0,0.999177;3.14159rad)
  sketch-geometry (6):
    g0: LineSegment [constr] StartX=0 StartY=0.85 StartZ=0 EndX=0 EndY=-0.85 EndZ=0
    g1: LineSegment StartX=0 StartY=-0.85 StartZ=0 EndX=0.490748 EndY=0 EndZ=0
    g2: LineSegment StartX=0.490748 StartY=0 StartZ=0 EndX=0 EndY=0.85 EndZ=0
    g3: LineSegment StartX=0 StartY=0.85 StartZ=0 EndX=-0.490748 EndY=1.7 EndZ=0
    g4: LineSegment StartX=-0.490748 StartY=1.7 StartZ=0 EndX=-0.490748 EndY=-1.7 EndZ=0
    g5: LineSegment StartX=-0.490748 StartY=-1.7 StartZ=0 EndX=0 EndY=-0.85 EndZ=0
  constraints (17):
    c: PointOnObject(g0,g-2)
    c: PointOnObject(g0,g-2)
    c: Coincident(g1,g0)
    c: PointOnObject(g1,g-1)
    c: Coincident(g2,g1)
    c: Coincident(g2,g0)
    c: Equal(g2,g1)
    c: Angle(g2,g1) = 2.0944
    c: Coincident(g0,g3)
    c: Coincident(g3,g4)
    c: Vertical(g4)
    c: Coincident(g4,g5)
    c: Coincident(g5,g0)
    c: Parallel(g5,g1)
    c: Equal(g5,g1)
    c: Parallel(g3,g2)
    c: Equal(g4,g-5)
FEATURE [PartDesign::SubtractivePipe] SubtractivePipe001  label="Left lens groove"
  AuxilleryCurvelinear = true
  AuxillerySpineTangent = false
  BaseFeature = -> SubtractivePipe
  Binormal = (0,0,0)
  Mode = 0
  Placement = pos=(0,0,0) rot=(1,0,0;1.5708rad)
  Profile = -> Sketch016
  Spine = -> Sketch014 [Edge2]
  SpineTangent = false
  Suppressed = false
  Transformation = 0
  Transition = 0
FEATURE [PartDesign::Body] Body
  AllowCompound = false
  Group = -> [Sketch,Pad,Sketch001,Sketch002,DatumPlane,Sketch003,Pad001,Sketch010,Pocket002,Sketch011,Pocket003,Fillet,Sketch008,Sketch012,DatumPlane003,Sketch017,Pad003,Sketch013,DatumPlane004,DatumPlane005,DatumLine001,Sketch018,Sketch019,AdditiveLoft,Mirrored,Pocket,Sketch014,DatumPlane001,Sketch015,SubtractivePipe,DatumPlane002,Sketch016,SubtractivePipe001]
  Origin = -> Origin
  Tip = -> SubtractivePipe001
FEATURE [App::Point] Origin001  label="Origin"
  Role = Origin
---- part left_temple.FCStd = doc fcstd_11b7f681f36e ----
FCSTD DOCUMENT  (FreeCAD 1.1R39679 (Git))
Label: left_temple
License: All rights reserved
LicenseURL: http://en.wikipedia.org/wiki/All_rights_reserved
objects: Sketcher::SketchObject×14, PartDesign::Plane×7, PartDesign::Line×3, PartDesign::Pocket×3, PartDesign::AdditiveLoft×2, App::Point×2, PartDesign::Pad×1, PartDesign::SubtractiveLoft×1, PartDesign::AdditivePipe×1, PartDesign::Fillet×1, PartDesign::Body×1, App::Part×1, Part::Mirroring×1
note: 67 computed .brp shape members not serialized (recipe doc carries the construction recipe); baked Part::Feature solids carry a one-line shape summary decoded from their .brp

FEATURE [Sketcher::SketchObject] Sketch001  label="Hinge mid profile master sketch"
  ArcFitTolerance = 1e-06
  AttachmentSupport = -> [XY_Plane001]
  ExternalTypes = [0]
  FullyConstrained = true
  MakeInternals = false
  MapMode = 5
  sketch-geometry (19):
    g0: ArcOfCircle CenterX=3e-16 CenterY=5.10698e-11 CenterZ=0 NormalX=0 NormalY=0 NormalZ=1 AngleXU=0 Radius=1.5 StartAngle=1.5708 EndAngle=3.52097
    g1: Circle CenterX=3e-16 CenterY=5.10698e-11 CenterZ=0 NormalX=0 NormalY=0 NormalZ=1 AngleXU=0 Radius=1.5
    g2: LineSegment StartX=18.3344 StartY=-85 StartZ=0 EndX=2.5 EndY=5.10738e-11 EndZ=0
    g3: ArcOfCircle CenterX=-95.7553 CenterY=-38.1767 CenterZ=0 NormalX=0 NormalY=0 NormalZ=1 AngleXU=0 Radius=101.585 StartAngle=0.184176 EndAngle=0.379377
    g4: LineSegment StartX=4.11175 StartY=-19.5728 StartZ=0 EndX=16.3682 EndY=-85.3663 EndZ=0
    g5: LineSegment StartX=16.3682 StartY=-85.3663 StartZ=0 EndX=18.3344 EndY=-85 EndZ=0
    g6: LineSegment StartX=3e-16 StartY=1.5 StartZ=0 EndX=0.1 EndY=1.5 EndZ=0
    g7: LineSegment StartX=0.1 StartY=1.5 StartZ=0 EndX=0.1 EndY=3.5 EndZ=0
    g8: ArcOfEllipse CenterX=0.1 CenterY=-2.08213 CenterZ=0 NormalX=0 NormalY=0 NormalZ=1 MajorRadius=5.58213 MinorRadius=2.58668 AngleXU=1.5708 StartAngle=5.09463 EndAngle=6.28318
    g9: LineSegment [constr] StartX=0.1 StartY=3.5 StartZ=0 EndX=-1.9 EndY=3.5 EndZ=0
    g10: GeomPoint [constr] X=0.0999963 Y=3.5 Z=0
    g11: Circle CenterX=3e-16 CenterY=5.10698e-11 CenterZ=0 NormalX=0 NormalY=0 NormalZ=1 AngleXU=0 Radius=0.55
    g12: LineSegment StartX=4.11175 StartY=-19.5728 StartZ=0 EndX=0.186162 EndY=1.5 EndZ=0
    g13: LineSegment StartX=0.1 StartY=1.5 StartZ=0 EndX=0.186162 EndY=1.5 EndZ=0
    g14: LineSegment [constr] StartX=-112.4 StartY=0 StartZ=0 EndX=-128.7 EndY=-85 EndZ=0
    g15: LineSegment [constr] StartX=16.3682 StartY=-85.3663 StartZ=0 EndX=16.3 EndY=-85 EndZ=0
    g16: LineSegment [constr] StartX=-128.7 StartY=-85 StartZ=0 EndX=-112.4 EndY=-85 EndZ=0
    g17: LineSegment [constr] StartX=-112.4 StartY=-85 StartZ=0 EndX=0 EndY=-85 EndZ=0
    g18: LineSegment [constr] StartX=0 StartY=-85 StartZ=0 EndX=16.3 EndY=-85 EndZ=0
  constraints (55):
    c: Equal(g1,g0)
    c: Diameter(g1) = 3
    c: Horizontal(g2,g0)
    c: Distance(g2,g1) = 1
    c: PointOnObject(g0,g-2)
    c: Coincident(g1,g0)
    c: Vertical(g0,g0)
    c: PointOnObject(g0,g-1)
    c: Tangent(g3,g0) = 1.5708
    c: Distance(g2,g4) = 2
    c: Tangent(g4,g3) = 1.5708
    c: Coincident(g5,g4)
    c: Coincident(g5,g2)
    c: Coincident(g6,g0)
    c: Coincident(g7,g6)
    c: Horizontal(g6)
    c: Vertical(g7)
    c: Distance(g7,g-2) = 0.1
    c: DistanceY(g7,g7) = 2
    c: Coincident(g8,g7)
    c: PointOnObject(g8,g7)
    c: Coincident(g9,g7)
    c: Horizontal(g9)
    c: Equal(g7,g9)
    c: Tangent(g8,g2) = -1.5708
    c: PointOnObject(g10,g8)
    c: PointOnObject(g10,g9)
    c: Tangent(g8,g9,g10) = -1.5708
    c: Coincident(g11,g0)
    c: Diameter(g11) = 1.1
    c: Coincident(g12,g3)
    c: Coincident(g13,g6)
    c: Coincident(g13,g12)
    c: Horizontal(g13)
    c: Parallel(g4,g2)
    c: Parallel(g12,g4)
    c: PointOnObject(g14,g-1)
    c: DistanceX(g14,g0) = 112.4
    c: Perpendicular(g4,g5)
    c: Coincident(g15,g4)
    c: Parallel(g15,g4)
    c: Coincident(g14,g16)
    c: PointOnObject(g17,g-2)
    c: Coincident(g17,g18)
    c: Coincident(g18,g15)
    c: Parallel(g17,g18)
    c: Equal(g16,g18)
    c: Coincident(g17,g16)
    c: Vertical(g14,g16)
    c: Parallel(g16,g17)
    c: Horizontal(g17)
    c: Distance(g17,g-1) = 85
    c: DistanceX(g14,g15) = 145
    c: Distance(g0,g3) = 20
    c: PointOnObject(g2,g18)
FEATURE [PartDesign::Pad] Pad  label="Hinge outer, outsized"
  Direction = (0,0,1)
  Length = 30
  Length2 = 10
  Midplane = true
  Profile = -> Sketch001 [Edge9,Edge8,Edge7,Edge6,Edge10,Edge4,Edge5]
  ReferenceAxis = -> Sketch001 [N_Axis]
  Refine = true
  Suppressed = false
  Type = 0
FEATURE [Sketcher::SketchObject] Sketch  label="Hinge axis, outsized"
  ArcFitTolerance = 1e-06
  AttachmentSupport = -> [XZ_Plane]
  ExternalTypes = [0]
  FullyConstrained = true
  MakeInternals = false
  MapMode = 5
  Placement = pos=(0,0,0) rot=(1,0,0;1.5708rad)
  sketch-geometry (2):
    g0: LineSegment StartX=-1.29347 StartY=-5.60263 StartZ=0 EndX=1.29347 EndY=5.60263 EndZ=0
    g1: LineSegment StartX=-0.562378 StartY=-2.43593 StartZ=0 EndX=0.562378 EndY=2.43593 EndZ=0
  constraints (6):
    c: Symmetric(g0,g0,g-1)
    c: Distance(g0,g0) = 11.5
    c: Angle(g0,g-2) = 0.226893
    c: PointOnObject(g1,g0)
    c: Symmetric(g1,g1,g-1)
    c: Distance(g1,g1) = 5
FEATURE [PartDesign::Plane] DatumPlane001  label="Hinge inner top profile plane"
  AttachmentSupport = -> [Sketch]
  Length = 161.106
  MapMode = 7
  Placement = pos=(1.29347,1.2e-15,5.60263) rot=(0.704823,-0.704823,-0.080304;2.98133rad)
  ResizeMode = 0
  Width = 86.5936
FEATURE [PartDesign::Plane] DatumPlane002  label="Hinge inner bottom profile plane"
  AttachmentSupport = -> [Sketch]
  Length = 161.106
  MapMode = 7
  Placement = pos=(-1.29347,-1.2e-15,-5.60263) rot=(0.704823,-0.704823,-0.080304;2.98133rad)
  ResizeMode = 0
  Width = 86.5936
FEATURE [PartDesign::Line] DatumLine  label="Edge of hinge outer on hinge inner top profile plane"
  AttacherType = Attacher::AttachEngineLine
  AttachmentSupport = -> [DatumPlane001,Pad]
  Length = 20
  MapMode = 30
  Placement = pos=(0.494787,-0.156714,5.78702) rot=(-0.063777,0.690602,0.720418;3.27446rad)
  ResizeMode = 0
FEATURE [PartDesign::Line] DatumLine001  label="Edge of hinge outer lip on hinge inner top profile plane"
  AttacherType = Attacher::AttachEngineLine
  AttachmentSupport = -> [DatumPlane001,Pad]
  Length = 20
  MapMode = 30
  Placement = pos=(0.1,1.2e-15,5.87816) rot=(0,0.707107,0.707107;3.14159rad)
  ResizeMode = 0
FEATURE [PartDesign::Line] DatumLine002  label="Edge of hinge outer on hinge inner bottom profile plane"
  AttacherType = Attacher::AttachEngineLine
  AttachmentSupport = -> [DatumPlane002,Pad]
  Length = 20
  MapMode = 30
  Placement = pos=(0.403562,0.332985,-5.99442) rot=(-0.063777,0.690602,0.720418;3.27446rad)
  ResizeMode = 0
FEATURE [Sketcher::SketchObject] Sketch008
  ArcFitTolerance = 1e-06
  AttachmentSupport = -> [DatumPlane001]
  ExternalGeometry = -> [Sketch001,DatumLine,Pad,DatumLine001]
  ExternalTypes = [0]
  FullyConstrained = true
  MakeInternals = false
  MapMode = 5
  Placement = pos=(1.29347,1.2e-15,5.60263) rot=(0.704823,-0.704823,-0.080304;2.98133rad)
  sketch-geometry (6):
    g0: LineSegment StartX=-1.5 StartY=1.22486 StartZ=0 EndX=-1.5 EndY=1.13643 EndZ=0
    g1: LineSegment StartX=-1.5 StartY=1.13643 StartZ=0 EndX=19.5728 EndY=-2.89241 EndZ=0
    g2: LineSegment [constr] StartX=0 StartY=0 StartZ=0 EndX=1.5 EndY=0 EndZ=0
    g3: Circle [constr] CenterX=0 CenterY=0 CenterZ=0 NormalX=0 NormalY=0 NormalZ=1 AngleXU=0 Radius=1.5
    g4: ArcOfCircle CenterX=-0.273426 CenterY=-1.04374 CenterZ=0 NormalX=0 NormalY=0 NormalZ=1 AngleXU=0 Radius=2.57896 StartAngle=1.31459 EndAngle=2.06645
    g5: ArcOfCircle CenterX=74.488 CenterY=284.34 CenterZ=0 NormalX=0 NormalY=0 NormalZ=1 AngleXU=0 Radius=292.435 StartAngle=4.45618 EndAngle=4.52348
  constraints (16):
    c: PointOnObject(g0,g-6)
    c: PointOnObject(g1,g-5)
    c: Vertical(g-4,g1)
    c: PointOnObject(g0,g-5)
    c: PointOnObject(g0,g-6)
    c: Coincident(g1,g0)
    c: Coincident(g4,g0)
    c: PointOnObject(g0,g-7)
    c: Coincident(g2,g-1)
    c: PointOnObject(g2,g-3)
    c: Horizontal(g2)
    c: Coincident(g3,g2)
    c: PointOnObject(g2,g3)
    c: Tangent(g1,g5) = -1.5708
    c: Tangent(g4,g5) = 1.5708
    c: Tangent(g4,g3) = -1.5708
FEATURE [Sketcher::SketchObject] Sketch009
  ArcFitTolerance = 1e-06
  AttachmentSupport = -> [DatumPlane002]
  ExternalGeometry = -> [DatumLine002,Sketch001,Sketch008]
  ExternalTypes = [0]
  FullyConstrained = true
  MakeInternals = false
  MapMode = 5
  Placement = pos=(-1.29347,-1.2e-15,-5.60263) rot=(0.704823,-0.704823,-0.080304;2.98133rad)
  sketch-geometry (6):
    g0: LineSegment StartX=-1.5 StartY=-1.51855 StartZ=0 EndX=19.5728 EndY=-5.5474 EndZ=0
    g1: LineSegment StartX=-1.5 StartY=-2.99799e-11 StartZ=0 EndX=-1.5 EndY=-1.51855 EndZ=0
    g2: Circle [constr] CenterX=0 CenterY=0 CenterZ=0 NormalX=0 NormalY=0 NormalZ=1 AngleXU=0 Radius=1.5
    g3: LineSegment [constr] StartX=0 StartY=0 StartZ=0 EndX=1.5 EndY=0 EndZ=0
    g4: ArcOfCircle CenterX=-1.67367e-11 CenterY=-2.99799e-11 CenterZ=0 NormalX=0 NormalY=0 NormalZ=1 AngleXU=0 Radius=1.5 StartAngle=1.06163 EndAngle=3.14159
    g5: ArcOfCircle CenterX=31.3801 CenterY=56.2106 CenterZ=0 NormalX=0 NormalY=0 NormalZ=1 AngleXU=0 Radius=62.8766 StartAngle=4.20323 EndAngle=4.52348
  constraints (15):
    c: PointOnObject(g0,g-3)
    c: PointOnObject(g5,g-3)
    c: Vertical(g5,g-4)
    c: Tangent(g4,g-6) = -1.5708
    c: Coincident(g0,g1)
    c: Coincident(g1,g4)
    c: Vertical(g1)
    c: Coincident(g2,g-1)
    c: Coincident(g3,g2)
    c: PointOnObject(g3,g-5)
    c: Horizontal(g3)
    c: PointOnObject(g3,g2)
    c: Tangent(g0,g5) = -1.5708
    c: Tangent(g4,g5) = 1.5708
    c: Tangent(g4,g2) = -1.5708
FEATURE [PartDesign::AdditiveLoft] AdditiveLoft001  label="Hinger inner"
  BaseFeature = -> Pad
  Closed = false
  Profile = -> Sketch008
  Refine = true
  Ruled = false
  Sections = -> [Sketch009]
  Suppressed = false
FEATURE [Sketcher::SketchObject] Sketch010
  ArcFitTolerance = 1e-06
  AttachmentSupport = -> [DatumPlane001]
  ExternalGeometry = -> [Sketch001]
  ExternalTypes = [0]
  FullyConstrained = true
  MakeInternals = false
  MapMode = 5
  Placement = pos=(1.29347,1.2e-15,5.60263) rot=(0.704823,-0.704823,-0.080304;2.98133rad)
  sketch-geometry (2):
    g0: LineSegment [constr] StartX=0 StartY=0 StartZ=0 EndX=0.55 EndY=0 EndZ=0
    g1: Circle CenterX=0 CenterY=0 CenterZ=0 NormalX=0 NormalY=0 NormalZ=1 AngleXU=0 Radius=0.55
  constraints (5):
    c: Coincident(g0,g-1)
    c: PointOnObject(g0,g-3)
    c: Horizontal(g0)
    c: Coincident(g1,g0)
    c: PointOnObject(g0,g1)
FEATURE [PartDesign::Pocket] Pocket  label="Hinge pin hole"
  BaseFeature = -> AdditiveLoft001
  Direction = (0.224951,0,0.97437)
  Length = 5
  Length2 = 5
  Midplane = true
  Profile = -> Sketch010
  ReferenceAxis = -> Sketch010 [N_Axis]
  Suppressed = false
  Type = 1
FEATURE [PartDesign::Plane] DatumPlane003  label="Hinge inner middle top profile plane"
  AttachmentSupport = -> [Sketch]
  Length = 161.106
  MapMode = 7
  Placement = pos=(0.562378,5e-16,2.43593) rot=(0.704823,-0.704823,-0.080304;2.98133rad)
  ResizeMode = 0
  Width = 86.5936
FEATURE [PartDesign::Plane] DatumPlane004  label="Hinge inner middle bottom profile plane"
  AttachmentSupport = -> [Sketch]
  Length = 161.106
  MapMode = 7
  Placement = pos=(-0.562378,-5e-16,-2.43593) rot=(0.704823,-0.704823,-0.080304;2.98133rad)
  ResizeMode = 0
  Width = 86.5936
FEATURE [Sketcher::SketchObject] Sketch011
  ArcFitTolerance = 1e-06
  AttachmentSupport = -> [DatumPlane003]
  ExternalGeometry = -> [Sketch001]
  ExternalTypes = [0]
  FullyConstrained = true
  MakeInternals = false
  MapMode = 5
  Placement = pos=(0.562378,5e-16,2.43593) rot=(0.704823,-0.704823,-0.080304;2.98133rad)
  sketch-geometry (8):
    g0: ArcOfCircle CenterX=0 CenterY=0 CenterZ=0 NormalX=0 NormalY=0 NormalZ=1 AngleXU=0 Radius=1.65 StartAngle=3.14159 EndAngle=5.23096
    g1: LineSegment [constr] StartX=1.5 StartY=0 StartZ=0 EndX=0 EndY=0 EndZ=0
    g2: LineSegment StartX=-1.65 StartY=2.5 StartZ=0 EndX=7.70983 EndY=2.5 EndZ=0
    g3: LineSegment StartX=-1.65 StartY=0 StartZ=0 EndX=-1.65 EndY=2.5 EndZ=0
    g4: LineSegment [constr] StartX=0.743463 StartY=-1.30279 StartZ=0 EndX=0.81781 EndY=-1.43307 EndZ=0
    g5: Circle [constr] CenterX=0 CenterY=0 CenterZ=0 NormalX=0 NormalY=0 NormalZ=1 AngleXU=0 Radius=1.5
    g6: LineSegment StartX=0.81781 StartY=-1.43307 StartZ=0 EndX=7.70983 EndY=2.5 EndZ=0
    g7: LineSegment [constr] StartX=0 StartY=1.5 StartZ=0 EndX=0 EndY=2.5 EndZ=0
  constraints (23):
    c: Coincident(g0,g-1)
    c: Coincident(g1,g0)
    c: Horizontal(g2)
    c: Coincident(g3,g2)
    c: Vertical(g3)
    c: PointOnObject(g1,g-3)
    c: PointOnObject(g1,g-1)
    c: PointOnObject(g0,g-1)
    c: Coincident(g3,g0)
    c: Coincident(g4,g0)
    c: Coincident(g5,g0)
    c: PointOnObject(g1,g5)
    c: PointOnObject(g4,g5)
    c: Coincident(g6,g2)
    c: Tangent(g6,g0) = -1.5708
    c: Distance(g4,g0) = 0.15
    c: PointOnObject(g7,g5)
    c: PointOnObject(g7,g2)
    c: PointOnObject(g0,g7)
    c: Vertical(g7)
    c: DistanceY(g7,g7) = 1
    c: PointOnObject(g0,g4)
    c: Angle(g-4,g6) = 0.698132
FEATURE [Sketcher::SketchObject] Sketch012
  ArcFitTolerance = 1e-06
  AttachmentSupport = -> [DatumPlane004]
  ExternalGeometry = -> [Sketch011]
  ExternalTypes = [0]
  FullyConstrained = true
  MakeInternals = false
  MapMode = 5
  Placement = pos=(-0.562378,-5e-16,-2.43593) rot=(0.704823,-0.704823,-0.080304;2.98133rad)
  sketch-geometry (4):
    g0: ArcOfCircle CenterX=0 CenterY=0 CenterZ=0 NormalX=0 NormalY=0 NormalZ=1 AngleXU=0 Radius=1.65 StartAngle=3.14159 EndAngle=5.23097
    g1: LineSegment StartX=-1.65 StartY=0 StartZ=0 EndX=-1.65 EndY=2.5 EndZ=0
    g2: LineSegment StartX=-1.65 StartY=2.5 StartZ=0 EndX=7.70983 EndY=2.5 EndZ=0
    g3: LineSegment StartX=7.70983 StartY=2.5 StartZ=0 EndX=0.817826 EndY=-1.43306 EndZ=0
  constraints (9):
    c: Coincident(g0,g-1)
    c: Coincident(g0,g-3)
    c: Coincident(g1,g-3)
    c: Coincident(g1,g-3)
    c: Coincident(g2,g1)
    c: Coincident(g2,g-4)
    c: Coincident(g3,g-4)
    c: Coincident(g3,g0)
    c: PointOnObject(g0,g-4)
FEATURE [PartDesign::SubtractiveLoft] SubtractiveLoft  label="Slot for frame hinge"
  BaseFeature = -> Pocket
  Closed = false
  Profile = -> Sketch011
  Ruled = false
  Sections = -> [Sketch012]
  Suppressed = false
FEATURE [Sketcher::SketchObject] Sketch013  label="Ear hook wire master sketch"
  ArcFitTolerance = 1e-06
  AttachmentSupport = -> [SubtractiveLoft]
  ExternalTypes = [0]
  FullyConstrained = true
  MakeInternals = false
  MapMode = 5
  Placement = pos=(0.449978,0.083825,0) rot=(0.648089,-0.538508,-0.538508;1.99153rad)
  sketch-geometry (10):
    g0: LineSegment StartX=0 StartY=0 StartZ=0 EndX=59.8128 EndY=-4.73606 EndZ=0
    g1: LineSegment StartX=59.8128 StartY=-4.73606 StartZ=0 EndX=69.7816 EndY=-5.52541 EndZ=0
    g2: LineSegment [constr] StartX=95.8971 StartY=-56.4408 StartZ=0 EndX=88.1428 EndY=-32.2204 EndZ=0
    g3: LineSegment StartX=69.7816 StartY=-5.52541 StartZ=0 EndX=90.9304 EndY=-7.2 EndZ=0
    g4: LineSegment StartX=95.8971 StartY=-56.4408 StartZ=0 EndX=95.7997 EndY=-56.4638 EndZ=0
    g5: ArcOfEllipse CenterX=88.1428 CenterY=-32.2204 CenterZ=0 NormalX=0 NormalY=0 NormalZ=1 MajorRadius=29.4 MinorRadius=25.1272 AngleXU=0.00824988 StartAngle=4.97225 EndAngle=7.75197
    g6: LineSegment [constr] StartX=117.542 StartY=-31.9779 StartZ=0 EndX=58.7438 EndY=-32.463 EndZ=0
    g7: GeomPoint [constr] X=103.406 Y=-32.0945 Z=0
    g8: GeomPoint [constr] X=72.8795 Y=-32.3463 Z=0
    g9: LineSegment [constr] StartX=117.543 StartY=-32.155 StartZ=0 EndX=117.543 EndY=-56.4408 EndZ=0
  constraints (27):
    c: Coincident(g-1,g0)
    c: Distance(g0,g0) = 60
    c: Coincident(g1,g0)
    c: Parallel(g0,g1)
    c: Distance(g1,g1) = 10
    c: Coincident(g2,g5)
    c: Parallel(g1,g3)
    c: Distance(g3,g-1) = 7.2
    c: Tangent(g4,g5) = 1.5708
    c: Distance(g4,g4) = 0.1
    c: InternalAlignment(g6,g5)
    c: InternalAlignment(g7,g5)
    c: InternalAlignment(g8,g5)
    c: Coincident(g1,g3)
    c: Coincident(g5,g2)
    c: Distance(g3,g3) = 21.215
    c: Distance(g2,g6) = 29.4
    c: Distance(g6,g3) = 22.6
    c: Tangent(g3,g5) = 1.5708
    c: Angle(g2,g3) = 1.18194
    c: Angle(g3,g6) = 0.0872665
    c: Tangent(g9,g5) = 1.5708
    c: Vertical(g9)
    c: Distance(g9,g-2) = 117.543
    c: Distance(g2,g-1) = 56.4408
    c: Distance(g4,g-2) = 95.7997
    c: Horizontal(g2,g9)
FEATURE [Sketcher::SketchObject] Sketch003
  ArcFitTolerance = 1e-06
  AttachmentSupport = -> [SubtractiveLoft]
  ExternalGeometry = -> [Sketch001,Sketch013,SubtractiveLoft]
  ExternalTypes = [0]
  FullyConstrained = true
  MakeInternals = false
  MapMode = 5
  Placement = pos=(0.449978,0.083825,0) rot=(0.506579,0.609663,0.609663;2.2038rad)
  sketch-geometry (10):
    g0: ArcOfCircle CenterX=-104.22 CenterY=556.093 CenterZ=0 NormalX=0 NormalY=0 NormalZ=1 AngleXU=0 Radius=560.584 StartAngle=4.79141 EndAngle=4.89667
    g1: LineSegment StartX=-86.9201 StartY=15 StartZ=0 EndX=-86.9201 EndY=-15 EndZ=0
    g2: ArcOfCircle CenterX=-13.0408 CenterY=-595.43 CenterZ=0 NormalX=0 NormalY=0 NormalZ=1 AngleXU=0 Radius=590.543 StartAngle=1.55125 EndAngle=1.64981
    g3: LineSegment StartX=-59.9707 StartY=-2.7423 StartZ=0 EndX=-59.6549 EndY=-6.72982 EndZ=0
    g4: LineSegment StartX=-86.9201 StartY=-15 StartZ=0 EndX=3.42249 EndY=-15 EndZ=0
    g5: LineSegment StartX=-1.5 StartY=5 StartZ=0 EndX=3.42249 EndY=5 EndZ=0
    g6: LineSegment StartX=3.42249 StartY=5 StartZ=0 EndX=3.42249 EndY=15 EndZ=0
    g7: LineSegment StartX=-1.5 StartY=-5 StartZ=0 EndX=3.42249 EndY=-5 EndZ=0
    g8: LineSegment StartX=3.42249 StartY=-15 StartZ=0 EndX=3.42249 EndY=-5 EndZ=0
    g9: LineSegment StartX=-86.9201 StartY=15 StartZ=0 EndX=3.42249 EndY=15 EndZ=0
  constraints (28):
    c: Coincident(g4,g1)
    c: Symmetric(g0,g2,g-4)
    c: Symmetric(g9,g4,g-4)
    c: Vertical(g0,g-3)
    c: Coincident(g5,g0)
    c: Coincident(g6,g5)
    c: Coincident(g6,g9)
    c: Horizontal(g5)
    c: Coincident(g7,g2)
    c: Horizontal(g7)
    c: Coincident(g8,g4)
    c: Coincident(g8,g7)
    c: Distance(g5,g7) = 10
    c: PointOnObject(g0,g3)
    c: PointOnObject(g2,g3)
    c: Coincident(g0,g3)
    c: Distance(g3,g3) = 4
    c: Coincident(g3,g2)
    c: Symmetric(g0,g2,g-5)
    c: PointOnObject(g-5,g3)
    c: Vertical(g1)
    c: Horizontal(g4)
    c: Coincident(g1,g9)
    c: Coincident(g1,g-6)
    c: PointOnObject(g-6,g9)
    c: Vertical(g6)
    c: Vertical(g8)
    c: PointOnObject(g-7,g6)
FEATURE [PartDesign::Pocket] Pocket001  label="Temple #1"
  BaseFeature = -> SubtractiveLoft
  Direction = (-0.983087,-0.183137,1e-16)
  Length = 5
  Length2 = 5
  Midplane = true
  Profile = -> Sketch003
  ReferenceAxis = -> Sketch003 [N_Axis]
  Refine = true
  Suppressed = false
  Type = 1
FEATURE [Sketcher::SketchObject] Sketch005
  ArcFitTolerance = 1e-06
  AttachmentSupport = -> [Pocket001]
  ExternalGeometry = -> [Sketch003]
  ExternalTypes = [0]
  FullyConstrained = true
  MakeInternals = false
  MapMode = 5
  Placement = pos=(0.449978,0.083825,0) rot=(0.506579,0.609663,0.609663;2.2038rad)
  sketch-geometry (10):
    g0: LineSegment [constr] StartX=-1.5 StartY=5 StartZ=0 EndX=0 EndY=5.27884 EndZ=0
    g1: LineSegment [constr] StartX=-1.5 StartY=2.96574 StartZ=0 EndX=0 EndY=3.24458 EndZ=0
    g2: LineSegment [constr] StartX=-1.5 StartY=-5 StartZ=0 EndX=0 EndY=-5.02947 EndZ=0
    g3: LineSegment [constr] StartX=-1.5 StartY=-2.99961 StartZ=0 EndX=0 EndY=-3.02909 EndZ=0
    g4: ArcOfCircle CenterX=-103.969 CenterY=554.188 CenterZ=0 NormalX=0 NormalY=0 NormalZ=1 AngleXU=0 Radius=560.665 StartAngle=4.79141 EndAngle=4.89619
    g5: LineSegment [constr] StartX=-59.9707 StartY=-2.7423 StartZ=0 EndX=-59.8128 EndY=-4.73606 EndZ=0
    g6: LineSegment [constr] StartX=-59.6549 StartY=-6.72982 StartZ=0 EndX=-59.8128 EndY=-4.73606 EndZ=0
    g7: LineSegment [constr] StartX=-59.8128 StartY=-4.73606 StartZ=0 EndX=-59.7131 EndY=-4.72817 EndZ=0
    g8: ArcOfCircle CenterX=-13.1011 CenterY=-593.401 CenterZ=0 NormalX=0 NormalY=0 NormalZ=1 AngleXU=0 Radius=590.516 StartAngle=1.55115 EndAngle=1.64981
    g9: LineSegment StartX=-1.5 StartY=2.96574 StartZ=0 EndX=-1.5 EndY=-2.99961 EndZ=0
  constraints (27):
    c: PointOnObject(g0,g-2)
    c: PointOnObject(g1,g-2)
    c: Parallel(g1,g0)
    c: Distance(g0,g1) = 2
    c: PointOnObject(g2,g-2)
    c: PointOnObject(g3,g-2)
    c: Parallel(g2,g3)
    c: Distance(g3,g2) = 2
    c: Coincident(g-3,g0)
    c: Coincident(g-4,g2)
    c: Coincident(g5,g-3)
    c: Coincident(g6,g-4)
    c: Coincident(g6,g5)
    c: Coincident(g7,g5)
    c: Parallel(g6,g5)
    c: Distance(g7,g7) = 0.1
    c: Equal(g5,g6)
    c: Perpendicular(g5,g7)
    c: Tangent(g7,g4) = -1.5708
    c: Coincident(g4,g8)
    c: Tangent(g8,g7)
    c: Tangent(g4,g1) = -1.5708
    c: Tangent(g8,g3) = 1.5708
    c: Vertical(g1,g0)
    c: Vertical(g3,g2)
    c: Coincident(g9,g1)
    c: Coincident(g9,g3)
FEATURE [PartDesign::Pocket] Pocket002  label="Temple #2"
  BaseFeature = -> Pocket001
  Direction = (-0.983087,-0.183137,1e-16)
  Length = 5
  Length2 = 5
  Midplane = true
  Profile = -> Sketch005
  ReferenceAxis = -> Sketch005 [N_Axis]
  Refine = true
  Suppressed = false
  Type = 1
FEATURE [PartDesign::Plane] DatumPlane  label="Ear hook wire root plane"
  AttachmentOffset = pos=(0,0,10) rot=(0,0,1;0rad)
  AttachmentSupport = -> [Pocket002,Sketch013]
  Length = 109.889
  MapMode = 6
  Placement = pos=(13.2295,-68.5176,-5.52541) rot=(0.62695,-0.520943,0.579269;2.2444rad)
  ResizeMode = 0
  Width = 91.8162
FEATURE [Sketcher::SketchObject] Sketch006  label="Ear hook wire root profile"
  ArcFitTolerance = 1e-06
  AttachmentSupport = -> [DatumPlane]
  ExternalGeometry = -> [Pocket002]
  ExternalTypes = [0]
  FullyConstrained = true
  MakeInternals = false
  MapMode = 5
  Placement = pos=(13.2295,-68.5176,-5.52541) rot=(0.62695,-0.520943,0.579269;2.2444rad)
  sketch-geometry (4):
    g0: LineSegment StartX=-1 StartY=-2 StartZ=0 EndX=1 EndY=-2 EndZ=0
    g1: ArcOfCircle CenterX=-1 CenterY=-1 CenterZ=0 NormalX=0 NormalY=0 NormalZ=1 AngleXU=0 Radius=1 StartAngle=1.5708 EndAngle=4.71239
    g2: ArcOfCircle CenterX=1 CenterY=-1 CenterZ=0 NormalX=0 NormalY=0 NormalZ=1 AngleXU=0 Radius=1 StartAngle=4.71239 EndAngle=7.85398
    g3: LineSegment StartX=-1 StartY=2.14e-14 StartZ=0 EndX=1 EndY=2.14e-14 EndZ=0
  constraints (13):
    c: PointOnObject(g0,g-3)
    c: Symmetric(g0,g0,g-2)
    c: Coincident(g1,g0)
    c: Vertical(g1,g0)
    c: Vertical(g1,g1)
    c: Coincident(g2,g0)
    c: Vertical(g0,g2)
    c: Horizontal(g1,g2)
    c: Vertical(g2,g2)
    c: Coincident(g3,g1)
    c: Coincident(g3,g2)
    c: Distance(g3,g0) = 2
    c: Tangent(g1,g-4)
FEATURE [PartDesign::AdditiveLoft] AdditiveLoft  label="Temple-to-ear-hook transition"
  BaseFeature = -> Pocket002
  Closed = false
  Profile = -> Pocket002 [Face3]
  Refine = true
  Ruled = false
  Sections = -> [Sketch006]
  Suppressed = false
FEATURE [Sketcher::SketchObject] Sketch014  label="Ear hook wire center"
  ArcFitTolerance = 1e-06
  AttachmentSupport = -> [DatumPlane]
  ExternalGeometry = -> [Sketch006]
  ExternalTypes = [0]
  FullyConstrained = true
  MakeInternals = false
  MapMode = 5
  Placement = pos=(13.2295,-68.5176,-5.52541) rot=(0.62695,-0.520943,0.579269;2.2444rad)
  sketch-geometry (2):
    g0: LineSegment StartX=-1 StartY=2.49e-14 StartZ=0 EndX=-2e-16 EndY=-1 EndZ=0
    g1: LineSegment StartX=-2e-16 StartY=-1 StartZ=0 EndX=1 EndY=-2 EndZ=0
  constraints (5):
    c: Coincident(g0,g-4)
    c: Coincident(g1,g0)
    c: Coincident(g1,g-3)
    c: Equal(g0,g1)
    c: Parallel(g0,g1)
FEATURE [PartDesign::Plane] DatumPlane006  label="Ear hook wire center plane"
  AttachmentSupport = -> [Sketch014,AdditiveLoft]
  Length = 170.393
  MapMode = 6
  Placement = pos=(14.2126,-68.3344,-5.52541) rot=(0.648089,-0.538508,-0.538508;1.99153rad)
  ResizeMode = 0
  Width = 103.726
FEATURE [Sketcher::SketchObject] Sketch015  label="Ear hook wire path"
  ArcFitTolerance = 1e-06
  AttachmentSupport = -> [DatumPlane006]
  ExternalGeometry = -> [Sketch013]
  ExternalTypes = [0]
  FullyConstrained = true
  MakeInternals = false
  MapMode = 5
  Placement = pos=(14.2126,-68.3344,-5.52541) rot=(0.648089,-0.538508,-0.538508;1.99153rad)
  sketch-geometry (7):
    g0: ArcOfEllipse CenterX=18.3612 CenterY=-26.695 CenterZ=0 NormalX=0 NormalY=0 NormalZ=1 MajorRadius=29.4 MinorRadius=25.1272 AngleXU=-0.110955 StartAngle=5.07771 EndAngle=7.85398
    g1: LineSegment [constr] StartX=47.5804 StartY=-29.9504 StartZ=0 EndX=-10.858 EndY=-23.4396 EndZ=0
    g2: LineSegment [constr] StartX=21.1435 StartY=-1.72233 StartZ=0 EndX=15.5789 EndY=-51.6677 EndZ=0
    g3: GeomPoint [constr] X=33.5312 Y=-28.3851 Z=0
    g4: GeomPoint [constr] X=3.19124 Y=-25.0049 Z=0
    g5: LineSegment [constr] StartX=18.3612 StartY=-26.695 StartZ=0 EndX=26.1155 EndY=-50.9154 EndZ=0
    g6: LineSegment StartX=21.1435 StartY=-1.72233 StartZ=0 EndX=0 EndY=0 EndZ=0
  constraints (10):
    c: InternalAlignment(g1-g4 -> g0) x4
    c: Coincident(g0,g-4)
    c: Equal(g-4,g0)
    c: PointOnObject(g-3,g2)
    c: Coincident(g5,g0)
    c: Coincident(g5,g-5)
    c: PointOnObject(g0,g5)
    c: PointOnObject(g0,g2)
    c: Coincident(g6,g0)
    c: Coincident(g6,g-1)
FEATURE [PartDesign::Plane] DatumPlane007  label="Ear hook wire end plane"
  AttachmentSupport = -> [Sketch015]
  Length = 93.2814
  MapMode = 7
  Placement = pos=(19.011,-94.0924,-56.7081) rot=(-0.071456,0.773762,0.629433;3.25772rad)
  ResizeMode = 0
  Width = 128.39
FEATURE [Sketcher::SketchObject] Sketch016  label="Ear hook wire end profile"
  ArcFitTolerance = 1e-06
  AttachmentSupport = -> [DatumPlane007]
  ExternalTypes = [0]
  FullyConstrained = true
  MakeInternals = false
  MapMode = 5
  Placement = pos=(19.011,-94.0924,-56.7081) rot=(-0.071456,0.773762,0.629433;3.25772rad)
  sketch-geometry (4):
    g0: ArcOfCircle CenterX=0 CenterY=0.05 CenterZ=0 NormalX=0 NormalY=0 NormalZ=1 AngleXU=0 Radius=1 StartAngle=0 EndAngle=3.14159
    g1: ArcOfCircle CenterX=0 CenterY=-0.05 CenterZ=0 NormalX=0 NormalY=0 NormalZ=1 AngleXU=0 Radius=1 StartAngle=3.14159 EndAngle=6.28319
    g2: LineSegment StartX=-1 StartY=0.05 StartZ=0 EndX=-1 EndY=-0.05 EndZ=0
    g3: LineSegment StartX=1 StartY=0.05 StartZ=0 EndX=1 EndY=-0.05 EndZ=0
  constraints (13):
    c: Horizontal(g0,g0)
    c: Horizontal(g0,g0)
    c: Horizontal(g1,g1)
    c: Horizontal(g1,g1)
    c: Symmetric(g1,g0,g-1)
    c: Coincident(g2,g0)
    c: Coincident(g2,g1)
    c: Vertical(g2)
    c: Coincident(g0,g3)
    c: Coincident(g1,g3)
    c: Distance(g3,g2) = 2
    c: DistanceY(g2,g2) = 0.1
    c: PointOnObject(g0,g-2)
FEATURE [PartDesign::AdditivePipe] AdditivePipe  label="Ear hook wire"
  AuxilleryCurvelinear = true
  AuxillerySpineTangent = false
  BaseFeature = -> AdditiveLoft
  Binormal = (0,0,0)
  Mode = 0
  Profile = -> Sketch006
  Refine = true
  Sections = -> [Sketch016]
  Spine = -> Sketch015
  SpineTangent = false
  Suppressed = false
  Transformation = 1
  Transition = 0
FEATURE [PartDesign::Fillet] Fillet  label="Ear hook wire end"
  Base = -> AdditivePipe [Edge109]
  BaseFeature = -> AdditivePipe
  Radius = 0.95
  Refine = true
  SupportTransform = false
  Suppressed = false
  UseAllEdges = false
FEATURE [PartDesign::Body] Body
  AllowCompound = false
  Group = -> [Sketch001,Sketch003,Pad,Sketch,DatumPlane001,DatumPlane002,DatumLine,DatumLine001,DatumLine002,Sketch008,Sketch009,AdditiveLoft001,Sketch010,Pocket,DatumPlane003,DatumPlane004,Sketch011,Sketch012,SubtractiveLoft,Sketch013,Pocket001,Sketch005,Pocket002,DatumPlane,Sketch006,AdditiveLoft,Sketch014,DatumPlane006,Sketch015,DatumPlane007,Sketch016,AdditivePipe,Fillet]
  Origin = -> Origin001
  Tip = -> Fillet
FEATURE [App::Part] Part  label="Right temple"
  Group = -> [Body]
  Origin = -> Origin
FEATURE [Part::Mirroring] Part__Mirroring  label="Left temple"
  Base = (0,0,0)
  Normal = (1,0,0)
  Source = -> Part
FEATURE [App::Point] Origin002  label="Origin"
  Role = Origin
FEATURE [App::Point] Origin003  label="Origin"
  Role = Origin
---- part lens_example.FCStd = doc fcstd_29e131de4cbf ----
FCSTD DOCUMENT  (FreeCAD 1.1R39029 (Git))
Label: lens_example
License: All rights reserved
LicenseURL: http://en.wikipedia.org/wiki/All_rights_reserved
objects: Sketcher::SketchObject×7, PartDesign::Plane×2, PartDesign::Pocket×2, PartDesign::Line×1, PartDesign::Revolution×1, PartDesign::AdditivePipe×1, PartDesign::Body×1, App::Part×1
note: 30 computed .brp shape members not serialized (recipe doc carries the construction recipe); baked Part::Feature solids carry a one-line shape summary decoded from their .brp

FEATURE [Sketcher::SketchObject] Sketch  label="Relative horizontal position of blank with respect to final cut lens' front face edge"
  ArcFitTolerance = 1e-06
  AttachmentSupport = -> [XY_Plane001]
  FullyConstrained = true
  MakeInternals = false
  MapMode = 5
  sketch-geometry (7):
    g0: LineSegment StartX=-6 StartY=0 StartZ=0 EndX=1.15e-14 EndY=-87.7496 EndZ=0
    g1: ArcOfCircle CenterX=1.15e-14 CenterY=-87.7496 CenterZ=0 NormalX=0 NormalY=0 NormalZ=1 AngleXU=0 Radius=90 StartAngle=1.23964 EndAngle=2.03849
    g2: LineSegment [constr] StartX=-40.5747 StartY=-7.41477 StartZ=0 EndX=1.42e-14 EndY=-87.7496 EndZ=0
    g3: LineSegment [constr] StartX=29.2622 StartY=-2.63958 StartZ=0 EndX=1.07e-14 EndY=-87.7496 EndZ=0
    g4: LineSegment [constr] StartX=-40.5747 StartY=-7.41477 StartZ=0 EndX=29.2622 EndY=-2.63958 EndZ=0
    g5: LineSegment StartX=-20 StartY=0 StartZ=0 EndX=20 EndY=0 EndZ=0
    g6: LineSegment StartX=0 StartY=0 StartZ=0 EndX=0 EndY=2.25036 EndZ=0
  constraints (21):
    c: PointOnObject(g0,g-1)
    c: Distance(g0,g-2) = 6
    c: Coincident(g1,g0)
    c: Coincident(g2,g1)
    c: Coincident(g2,g0)
    c: Coincident(g3,g1)
    c: Coincident(g3,g0)
    c: Coincident(g4,g1)
    c: Coincident(g4,g1)
    c: Perpendicular(g4,g0)
    c: PointOnObject(g5,g1)
    c: PointOnObject(g5,g1)
    c: PointOnObject(g5,g-1)
    c: Symmetric(g5,g5,g-2)
    c: Distance(g5,g5) = 40
    c: Distance(g4,g4) = 70
    c: Radius(g1) = 90
    c: Coincident(g6,g-1)
    c: PointOnObject(g6,g1)
    c: Distance(g6,g6) = 2.25036
    c: Vertical(g6)
FEATURE [PartDesign::Plane] DatumPlane  label="Blank's outer spherical lens' center's vertical plane"
  AttachmentOffset = pos=(0,0,0) rot=(0,1,0;1.5708rad)
  AttachmentSupport = -> [Sketch]
  Length = 129.305
  MapMode = 7
  Placement = pos=(1.24e-14,-87.7496,0) rot=(-0.60362,0.563756,0.563756;4.22775rad)
  ResizeMode = 0
  Width = 65.1124
FEATURE [PartDesign::Line] DatumLine  label="Cut lens' vertical center plane"
  AttacherType = Attacher::AttachEngineLine
  AttachmentSupport = -> [XZ_Plane001,DatumPlane]
  Length = 20
  MapMode = 30
  Placement = pos=(-6,7.1e-15,-4e-16) rot=(0,1,0;3.14159rad)
  ResizeMode = 0
FEATURE [Sketcher::SketchObject] Sketch001  label="Relative vertical position of blank with respect to final cut lens' front face edge"
  ArcFitTolerance = 1e-06
  AttachmentSupport = -> [DatumPlane]
  ExternalGeometry = -> [DatumLine]
  FullyConstrained = true
  MakeInternals = false
  MapMode = 5
  Placement = pos=(1.24e-14,-87.7496,0) rot=(0.60362,-0.563756,-0.563756;2.05544rad)
  sketch-geometry (4):
    g0: LineSegment StartX=-87.9545 StartY=5 StartZ=0 EndX=0 EndY=-4.4e-15 EndZ=0
    g1: ArcOfCircle CenterX=0 CenterY=-4.1e-15 CenterZ=0 NormalX=0 NormalY=0 NormalZ=1 AngleXU=0 Radius=89.9833 StartAngle=2.6853 EndAngle=3.48431
    g2: LineSegment [constr] StartX=-80.7774 StartY=39.6485 StartZ=0 EndX=-84.7504 EndY=-30.2387 EndZ=0
    g3: LineSegment StartX=-87.9545 StartY=19 StartZ=0 EndX=-87.9545 EndY=-19 EndZ=0
  constraints (13):
    c: PointOnObject(g0,g-3)
    c: Distance(g0,g-1) = 5
    c: Coincident(g1,g0)
    c: Coincident(g2,g1)
    c: Perpendicular(g2,g0)
    c: Coincident(g2,g1)
    c: Distance(g2,g2) = 70
    c: PointOnObject(g3,g1)
    c: PointOnObject(g3,g1)
    c: Symmetric(g3,g3,g-1)
    c: PointOnObject(g3,g-3)
    c: DistanceY(g3,g3) = 38
    c: PointOnObject(g0,g-2)
FEATURE [Sketcher::SketchObject] Sketch002
  ArcFitTolerance = 1e-06
  AttachmentSupport = -> [DatumPlane]
  ExternalGeometry = -> [Sketch001]
  FullyConstrained = true
  MakeInternals = false
  MapMode = 5
  Placement = pos=(1.24e-14,-87.7496,0) rot=(0.60362,-0.563756,-0.563756;2.05544rad)
  sketch-geometry (4):
    g0: ArcOfCircle CenterX=-14.9592 CenterY=0.850393 CenterZ=0 NormalX=0 NormalY=0 NormalZ=1 AngleXU=0 Radius=73 StartAngle=2.58478 EndAngle=3.08481
    g1: LineSegment StartX=-80.7774 StartY=39.6485 StartZ=0 EndX=-76.9319 EndY=39.4299 EndZ=0
    g2: ArcOfCircle CenterX=0 CenterY=0 CenterZ=0 NormalX=0 NormalY=0 NormalZ=1 AngleXU=0 Radius=89.9833 StartAngle=2.6853 EndAngle=3.08481
    g3: LineSegment StartX=-89.8383 StartY=5.10709 StartZ=0 EndX=-87.8415 EndY=4.99357 EndZ=0
  constraints (12):
    c: PointOnObject(g0,g-4)
    c: PointOnObject(g0,g-4)
    c: Radius(g0) = 73
    c: Coincident(g1,g-3)
    c: Coincident(g1,g0)
    c: Parallel(g-4,g1)
    c: Coincident(g2,g1)
    c: Coincident(g2,g-1)
    c: Coincident(g3,g2)
    c: Coincident(g3,g0)
    c: Parallel(g3,g-4)
    c: Distance(g2,g0) = 2
FEATURE [PartDesign::Revolution] Revolution  label="Lens blank"
  Angle = 360
  Angle2 = 60
  Axis = (0.0681071,-0.996062,-0.0567559)
  Base = (-6,0,5)
  Placement = pos=(1.24e-14,-87.7496,0) rot=(-0.60362,0.563756,0.563756;4.22775rad)
  Profile = -> Sketch002
  ReferenceAxis = -> Sketch001 [Edge1]
  Suppressed = false
  Type = 0
FEATURE [Sketcher::SketchObject] Sketch003
  ArcFitTolerance = 1e-06
  AttachmentSupport = -> [XZ_Plane001]
  ExternalGeometry = -> [Sketch,Sketch001]
  FullyConstrained = true
  MakeInternals = false
  MapMode = 5
  Placement = pos=(0,0,0) rot=(1,0,0;1.5708rad)
  sketch-geometry (6):
    g0: Ellipse CenterX=0 CenterY=0 CenterZ=0 NormalX=0 NormalY=0 NormalZ=1 MajorRadius=20 MinorRadius=19 AngleXU=-2.406e-13
    g1: LineSegment [constr] StartX=20 StartY=0 StartZ=0 EndX=-20 EndY=0 EndZ=0
    g2: LineSegment [constr] StartX=-4.938e-13 StartY=19 StartZ=0 EndX=4.938e-13 EndY=-19 EndZ=0
    g3: GeomPoint [constr] X=6.245 Y=-1.5025e-12 Z=0
    g4: GeomPoint [constr] X=-6.245 Y=1.5024e-12 Z=0
    g5: Circle CenterX=0 CenterY=0 CenterZ=0 NormalX=0 NormalY=0 NormalZ=1 AngleXU=0 Radius=75
  constraints (6):
    c: InternalAlignment(g1-g4 -> g0) x4
    c: Coincident(g0,g-1)
    c: Coincident(g-3,g1)
    c: Horizontal(g2,g-4)
    c: Coincident(g5,g0)
    c: Diameter(g5) = 150
FEATURE [PartDesign::Pocket] Pocket  label="Cut lens"
  BaseFeature = -> Revolution
  Direction = (0,1,-2e-16)
  Length = 5
  Length2 = 5
  Midplane = true
  Placement = pos=(1.24e-14,-87.7496,0) rot=(-0.60362,0.563756,0.563756;4.22775rad)
  Profile = -> Sketch003
  ReferenceAxis = -> Sketch003 [N_Axis]
  Suppressed = false
  Type = 1
FEATURE [PartDesign::Plane] DatumPlane001  label="Bevel edge plane"
  AttachmentOffset = pos=(0,0,1) rot=(0,0,1;0rad)
  AttachmentSupport = -> [XZ_Plane001]
  Length = 60
  MapMode = 5
  Placement = pos=(0,-1,2e-16) rot=(1,0,0;1.5708rad)
  ResizeMode = 0
  Width = 60
FEATURE [Sketcher::SketchObject] Sketch004
  ArcFitTolerance = 1e-06
  AttachmentSupport = -> [XY_Plane001]
  ExternalGeometry = -> [Sketch003,DatumPlane001]
  FullyConstrained = true
  MakeInternals = false
  MapMode = 5
  sketch-geometry (5):
    g0: LineSegment StartX=20 StartY=-0.15 StartZ=0 EndX=20.4907 EndY=-1 EndZ=0
    g1: LineSegment StartX=20 StartY=-1.85 StartZ=0 EndX=20.4907 EndY=-1 EndZ=0
    g2: LineSegment [constr] StartX=20 StartY=7.474e-13 StartZ=0 EndX=20 EndY=-0.15 EndZ=0
    g3: LineSegment StartX=20 StartY=-0.15 StartZ=0 EndX=20 EndY=-1.85 EndZ=0
    g4: LineSegment [constr] StartX=20 StartY=-1.85 StartZ=0 EndX=20 EndY=-2 EndZ=0
  constraints (15):
    c: Coincident(g1,g0)
    c: Coincident(g2,g3)
    c: Vertical(g2)
    c: Coincident(g3,g4)
    c: Vertical(g3)
    c: Vertical(g4)
    c: Equal(g4,g2)
    c: DistanceY(g2,g2) = 0.15
    c: Coincident(g0,g2)
    c: Coincident(g3,g1)
    c: Equal(g0,g1)
    c: Angle(g0,g1) = 2.0944
    c: PointOnObject(g0,g-4)
    c: PointOnObject(g-3,g3)
    c: DistanceY(g4,g2) = 2
FEATURE [PartDesign::AdditivePipe] AdditivePipe  label="Bevel"
  AuxilleryCurvelinear = true
  AuxillerySpineTangent = false
  BaseFeature = -> Pocket
  Binormal = (0,0,0)
  Mode = 0
  Placement = pos=(1.24e-14,-87.7496,0) rot=(-0.60362,0.563756,0.563756;4.22775rad)
  Profile = -> Sketch004 [?Edge2]
  Spine = -> Sketch003 [Edge1]
  SpineTangent = false
  Suppressed = false
  Transformation = 0
  Transition = 0
FEATURE [Sketcher::SketchObject] Sketch005
  ArcFitTolerance = 1e-06
  AttachmentSupport = -> [XZ_Plane001]
  ExternalGeometry = -> [Sketch003,Sketch004]
  FullyConstrained = true
  MakeInternals = false
  MapMode = 5
  Placement = pos=(0,0,0) rot=(1,0,0;1.5708rad)
  sketch-geometry (4):
    g0: LineSegment StartX=19.9369 StartY=1.5081 StartZ=0 EndX=20.4907 EndY=1.55 EndZ=0
    g1: LineSegment StartX=20.4907 StartY=1.55 StartZ=0 EndX=20.4907 EndY=-1.55 EndZ=0
    g2: LineSegment StartX=20.4907 StartY=-1.55 StartZ=0 EndX=19.9369 EndY=-1.5081 EndZ=0
    g3: LineSegment StartX=19.9369 StartY=1.5081 StartZ=0 EndX=19.9369 EndY=-1.5081 EndZ=0
  constraints (12):
    c: Coincident(g1,g0)
    c: Vertical(g1)
    c: Coincident(g2,g1)
    c: Vertical(g2,g0)
    c: DistanceY(g1,g1) = 3.1
    c: Coincident(g3,g0)
    c: Coincident(g3,g2)
    c: PointOnObject(g0,g-3)
    c: PointOnObject(g2,g-3)
    c: PointOnObject(g-1,g0)
    c: PointOnObject(g-1,g2)
    c: PointOnObject(g-4,g1)
FEATURE [PartDesign::Pocket] Pocket001  label="Registration notch"
  BaseFeature = -> AdditivePipe
  Direction = (0,1,-2e-16)
  Length = 5
  Length2 = 5
  Midplane = true
  Placement = pos=(1.24e-14,-87.7496,0) rot=(-0.60362,0.563756,0.563756;4.22775rad)
  Profile = -> Sketch005
  ReferenceAxis = -> Sketch005 [N_Axis]
  Suppressed = false
  Type = 1
FEATURE [Sketcher::SketchObject] Sketch006  label="Lens center marker"
  ArcFitTolerance = 1e-06
  AttachmentSupport = -> [DatumPlane001]
  FullyConstrained = true
  MakeInternals = false
  MapMode = 5
  Placement = pos=(0,-1,2e-16) rot=(1,0,0;1.5708rad)
  sketch-geometry (1):
    g0: Circle CenterX=0 CenterY=0 CenterZ=0 NormalX=0 NormalY=0 NormalZ=1 AngleXU=0 Radius=0.5
  constraints (2):
    c: Coincident(g0,g-1)
    c: Diameter(g0) = 1
FEATURE [PartDesign::Body] Body
  AllowCompound = false
  Group = -> [Sketch,DatumPlane,DatumLine,Sketch001,Sketch002,Revolution,Sketch003,Pocket,Sketch004,DatumPlane001,Sketch006,AdditivePipe,Sketch005,Pocket001]
  Origin = -> Origin001
  Tip = -> Pocket001
FEATURE [App::Part] Part
  Group = -> [Body]
  Origin = -> Origin
---- part right_temple.FCStd = doc fcstd_3b536f3ea897 ----
FCSTD DOCUMENT  (FreeCAD 1.1R39679 (Git))
Label: right_temple
License: All rights reserved
LicenseURL: http://en.wikipedia.org/wiki/All_rights_reserved
objects: Sketcher::SketchObject×14, PartDesign::Plane×7, PartDesign::Line×3, PartDesign::Pocket×3, PartDesign::AdditiveLoft×2, App::Point×2, PartDesign::Pad×1, PartDesign::SubtractiveLoft×1, PartDesign::AdditivePipe×1, PartDesign::Fillet×1, PartDesign::Body×1, App::Part×1
note: 66 computed .brp shape members not serialized (recipe doc carries the construction recipe); baked Part::Feature solids carry a one-line shape summary decoded from their .brp

FEATURE [Sketcher::SketchObject] Sketch001  label="Hinge mid profile master sketch"
  ArcFitTolerance = 1e-06
  AttachmentSupport = -> [XY_Plane001]
  ExternalTypes = [0]
  FullyConstrained = true
  MakeInternals = false
  MapMode = 5
  sketch-geometry (19):
    g0: ArcOfCircle CenterX=3e-16 CenterY=5.10698e-11 CenterZ=0 NormalX=0 NormalY=0 NormalZ=1 AngleXU=0 Radius=1.5 StartAngle=1.5708 EndAngle=3.52097
    g1: Circle CenterX=3e-16 CenterY=5.10698e-11 CenterZ=0 NormalX=0 NormalY=0 NormalZ=1 AngleXU=0 Radius=1.5
    g2: LineSegment StartX=18.3344 StartY=-85 StartZ=0 EndX=2.5 EndY=5.10738e-11 EndZ=0
    g3: ArcOfCircle CenterX=-95.7553 CenterY=-38.1767 CenterZ=0 NormalX=0 NormalY=0 NormalZ=1 AngleXU=0 Radius=101.585 StartAngle=0.184176 EndAngle=0.379377
    g4: LineSegment StartX=4.11175 StartY=-19.5728 StartZ=0 EndX=16.3682 EndY=-85.3663 EndZ=0
    g5: LineSegment StartX=16.3682 StartY=-85.3663 StartZ=0 EndX=18.3344 EndY=-85 EndZ=0
    g6: LineSegment StartX=3e-16 StartY=1.5 StartZ=0 EndX=0.1 EndY=1.5 EndZ=0
    g7: LineSegment StartX=0.1 StartY=1.5 StartZ=0 EndX=0.1 EndY=3.5 EndZ=0
    g8: ArcOfEllipse CenterX=0.1 CenterY=-2.08213 CenterZ=0 NormalX=0 NormalY=0 NormalZ=1 MajorRadius=5.58213 MinorRadius=2.58668 AngleXU=1.5708 StartAngle=5.09463 EndAngle=6.28318
    g9: LineSegment [constr] StartX=0.1 StartY=3.5 StartZ=0 EndX=-1.9 EndY=3.5 EndZ=0
    g10: GeomPoint [constr] X=0.0999963 Y=3.5 Z=0
    g11: Circle CenterX=3e-16 CenterY=5.10698e-11 CenterZ=0 NormalX=0 NormalY=0 NormalZ=1 AngleXU=0 Radius=0.55
    g12: LineSegment StartX=4.11175 StartY=-19.5728 StartZ=0 EndX=0.186162 EndY=1.5 EndZ=0
    g13: LineSegment StartX=0.1 StartY=1.5 StartZ=0 EndX=0.186162 EndY=1.5 EndZ=0
    g14: LineSegment [constr] StartX=-112.4 StartY=0 StartZ=0 EndX=-128.7 EndY=-85 EndZ=0
    g15: LineSegment [constr] StartX=16.3682 StartY=-85.3663 StartZ=0 EndX=16.3 EndY=-85 EndZ=0
    g16: LineSegment [constr] StartX=-128.7 StartY=-85 StartZ=0 EndX=-112.4 EndY=-85 EndZ=0
    g17: LineSegment [constr] StartX=-112.4 StartY=-85 StartZ=0 EndX=0 EndY=-85 EndZ=0
    g18: LineSegment [constr] StartX=0 StartY=-85 StartZ=0 EndX=16.3 EndY=-85 EndZ=0
  constraints (55):
    c: Equal(g1,g0)
    c: Diameter(g1) = 3
    c: Horizontal(g2,g0)
    c: Distance(g2,g1) = 1
    c: PointOnObject(g0,g-2)
    c: Coincident(g1,g0)
    c: Vertical(g0,g0)
    c: PointOnObject(g0,g-1)
    c: Tangent(g3,g0) = 1.5708
    c: Distance(g2,g4) = 2
    c: Tangent(g4,g3) = 1.5708
    c: Coincident(g5,g4)
    c: Coincident(g5,g2)
    c: Coincident(g6,g0)
    c: Coincident(g7,g6)
    c: Horizontal(g6)
    c: Vertical(g7)
    c: Distance(g7,g-2) = 0.1
    c: DistanceY(g7,g7) = 2
    c: Coincident(g8,g7)
    c: PointOnObject(g8,g7)
    c: Coincident(g9,g7)
    c: Horizontal(g9)
    c: Equal(g7,g9)
    c: Tangent(g8,g2) = -1.5708
    c: PointOnObject(g10,g8)
    c: PointOnObject(g10,g9)
    c: Tangent(g8,g9,g10) = -1.5708
    c: Coincident(g11,g0)
    c: Diameter(g11) = 1.1
    c: Coincident(g12,g3)
    c: Coincident(g13,g6)
    c: Coincident(g13,g12)
    c: Horizontal(g13)
    c: Parallel(g4,g2)
    c: Parallel(g12,g4)
    c: PointOnObject(g14,g-1)
    c: DistanceX(g14,g0) = 112.4
    c: Perpendicular(g4,g5)
    c: Coincident(g15,g4)
    c: Parallel(g15,g4)
    c: Coincident(g14,g16)
    c: PointOnObject(g17,g-2)
    c: Coincident(g17,g18)
    c: Coincident(g18,g15)
    c: Parallel(g17,g18)
    c: Equal(g16,g18)
    c: Coincident(g17,g16)
    c: Vertical(g14,g16)
    c: Parallel(g16,g17)
    c: Horizontal(g17)
    c: Distance(g17,g-1) = 85
    c: DistanceX(g14,g15) = 145
    c: Distance(g0,g3) = 20
    c: PointOnObject(g2,g18)
FEATURE [PartDesign::Pad] Pad  label="Hinge outer, outsized"
  Direction = (0,0,1)
  Length = 30
  Length2 = 10
  Midplane = true
  Profile = -> Sketch001 [Edge9,Edge8,Edge7,Edge6,Edge10,Edge4,Edge5]
  ReferenceAxis = -> Sketch001 [N_Axis]
  Refine = true
  Suppressed = false
  Type = 0
FEATURE [Sketcher::SketchObject] Sketch  label="Hinge axis, outsized"
  ArcFitTolerance = 1e-06
  AttachmentSupport = -> [XZ_Plane]
  ExternalTypes = [0]
  FullyConstrained = true
  MakeInternals = false
  MapMode = 5
  Placement = pos=(0,0,0) rot=(1,0,0;1.5708rad)
  sketch-geometry (2):
    g0: LineSegment StartX=-1.29347 StartY=-5.60263 StartZ=0 EndX=1.29347 EndY=5.60263 EndZ=0
    g1: LineSegment StartX=-0.562378 StartY=-2.43593 StartZ=0 EndX=0.562378 EndY=2.43593 EndZ=0
  constraints (6):
    c: Symmetric(g0,g0,g-1)
    c: Distance(g0,g0) = 11.5
    c: Angle(g0,g-2) = 0.226893
    c: PointOnObject(g1,g0)
    c: Symmetric(g1,g1,g-1)
    c: Distance(g1,g1) = 5
FEATURE [PartDesign::Plane] DatumPlane001  label="Hinge inner top profile plane"
  AttachmentSupport = -> [Sketch]
  Length = 160.885
  MapMode = 7
  Placement = pos=(1.29347,1.2e-15,5.60263) rot=(0.704823,-0.704823,-0.080304;2.98133rad)
  ResizeMode = 0
  Width = 84.0412
FEATURE [PartDesign::Plane] DatumPlane002  label="Hinge inner bottom profile plane"
  AttachmentSupport = -> [Sketch]
  Length = 160.885
  MapMode = 7
  Placement = pos=(-1.29347,-1.2e-15,-5.60263) rot=(0.704823,-0.704823,-0.080304;2.98133rad)
  ResizeMode = 0
  Width = 84.0412
FEATURE [PartDesign::Line] DatumLine  label="Edge of hinge outer on hinge inner top profile plane"
  AttacherType = Attacher::AttachEngineLine
  AttachmentSupport = -> [DatumPlane001,Pad]
  Length = 20
  MapMode = 30
  Placement = pos=(0.494787,-0.156714,5.78702) rot=(-0.063777,0.690602,0.720418;3.27446rad)
  ResizeMode = 0
FEATURE [PartDesign::Line] DatumLine001  label="Edge of hinge outer lip on hinge inner top profile plane"
  AttacherType = Attacher::AttachEngineLine
  AttachmentSupport = -> [DatumPlane001,Pad]
  Length = 20
  MapMode = 30
  Placement = pos=(0.1,1.2e-15,5.87816) rot=(0,0.707107,0.707107;3.14159rad)
  ResizeMode = 0
FEATURE [PartDesign::Line] DatumLine002  label="Edge of hinge outer on hinge inner bottom profile plane"
  AttacherType = Attacher::AttachEngineLine
  AttachmentSupport = -> [DatumPlane002,Pad]
  Length = 20
  MapMode = 30
  Placement = pos=(0.403562,0.332985,-5.99442) rot=(-0.063777,0.690602,0.720418;3.27446rad)
  ResizeMode = 0
FEATURE [Sketcher::SketchObject] Sketch008
  ArcFitTolerance = 1e-06
  AttachmentSupport = -> [DatumPlane001]
  ExternalGeometry = -> [Sketch001,DatumLine,Pad,DatumLine001]
  ExternalTypes = [0]
  FullyConstrained = true
  MakeInternals = false
  MapMode = 5
  Placement = pos=(1.29347,1.2e-15,5.60263) rot=(0.704823,-0.704823,-0.080304;2.98133rad)
  sketch-geometry (6):
    g0: LineSegment StartX=-1.5 StartY=1.22486 StartZ=0 EndX=-1.5 EndY=1.13643 EndZ=0
    g1: LineSegment StartX=-1.5 StartY=1.13643 StartZ=0 EndX=19.5728 EndY=-2.89241 EndZ=0
    g2: LineSegment [constr] StartX=0 StartY=0 StartZ=0 EndX=1.5 EndY=0 EndZ=0
    g3: Circle [constr] CenterX=0 CenterY=0 CenterZ=0 NormalX=0 NormalY=0 NormalZ=1 AngleXU=0 Radius=1.5
    g4: ArcOfCircle CenterX=-0.273426 CenterY=-1.04374 CenterZ=0 NormalX=0 NormalY=0 NormalZ=1 AngleXU=0 Radius=2.57896 StartAngle=1.31459 EndAngle=2.06645
    g5: ArcOfCircle CenterX=74.488 CenterY=284.34 CenterZ=0 NormalX=0 NormalY=0 NormalZ=1 AngleXU=0 Radius=292.435 StartAngle=4.45618 EndAngle=4.52348
  constraints (16):
    c: PointOnObject(g0,g-6)
    c: PointOnObject(g1,g-5)
    c: Vertical(g-4,g1)
    c: PointOnObject(g0,g-5)
    c: PointOnObject(g0,g-6)
    c: Coincident(g1,g0)
    c: Coincident(g4,g0)
    c: PointOnObject(g0,g-7)
    c: Coincident(g2,g-1)
    c: PointOnObject(g2,g-3)
    c: Horizontal(g2)
    c: Coincident(g3,g2)
    c: PointOnObject(g2,g3)
    c: Tangent(g1,g5) = -1.5708
    c: Tangent(g4,g5) = 1.5708
    c: Tangent(g4,g3) = -1.5708
FEATURE [Sketcher::SketchObject] Sketch009
  ArcFitTolerance = 1e-06
  AttachmentSupport = -> [DatumPlane002]
  ExternalGeometry = -> [DatumLine002,Sketch001,Sketch008]
  ExternalTypes = [0]
  FullyConstrained = true
  MakeInternals = false
  MapMode = 5
  Placement = pos=(-1.29347,-1.2e-15,-5.60263) rot=(0.704823,-0.704823,-0.080304;2.98133rad)
  sketch-geometry (6):
    g0: LineSegment StartX=-1.5 StartY=-1.51855 StartZ=0 EndX=19.5728 EndY=-5.5474 EndZ=0
    g1: LineSegment StartX=-1.5 StartY=-2.99788e-11 StartZ=0 EndX=-1.5 EndY=-1.51855 EndZ=0
    g2: Circle [constr] CenterX=0 CenterY=0 CenterZ=0 NormalX=0 NormalY=0 NormalZ=1 AngleXU=0 Radius=1.5
    g3: LineSegment [constr] StartX=0 StartY=0 StartZ=0 EndX=1.5 EndY=0 EndZ=0
    g4: ArcOfCircle CenterX=-1.67359e-11 CenterY=-2.99788e-11 CenterZ=0 NormalX=0 NormalY=0 NormalZ=1 AngleXU=0 Radius=1.5 StartAngle=1.06163 EndAngle=3.14159
    g5: ArcOfCircle CenterX=31.3801 CenterY=56.2106 CenterZ=0 NormalX=0 NormalY=0 NormalZ=1 AngleXU=0 Radius=62.8766 StartAngle=4.20323 EndAngle=4.52348
  constraints (15):
    c: PointOnObject(g0,g-3)
    c: PointOnObject(g5,g-3)
    c: Vertical(g5,g-4)
    c: Tangent(g4,g-6) = -1.5708
    c: Coincident(g0,g1)
    c: Coincident(g1,g4)
    c: Vertical(g1)
    c: Coincident(g2,g-1)
    c: Coincident(g3,g2)
    c: PointOnObject(g3,g-5)
    c: Horizontal(g3)
    c: PointOnObject(g3,g2)
    c: Tangent(g0,g5) = -1.5708
    c: Tangent(g4,g5) = 1.5708
    c: Tangent(g4,g2) = -1.5708
FEATURE [PartDesign::AdditiveLoft] AdditiveLoft001  label="Hinger inner"
  BaseFeature = -> Pad
  Closed = false
  Profile = -> Sketch008
  Refine = true
  Ruled = false
  Sections = -> [Sketch009]
  Suppressed = false
FEATURE [Sketcher::SketchObject] Sketch010
  ArcFitTolerance = 1e-06
  AttachmentSupport = -> [DatumPlane001]
  ExternalGeometry = -> [Sketch001]
  ExternalTypes = [0]
  FullyConstrained = true
  MakeInternals = false
  MapMode = 5
  Placement = pos=(1.29347,1.2e-15,5.60263) rot=(0.704823,-0.704823,-0.080304;2.98133rad)
  sketch-geometry (2):
    g0: LineSegment [constr] StartX=0 StartY=0 StartZ=0 EndX=0.55 EndY=0 EndZ=0
    g1: Circle CenterX=0 CenterY=0 CenterZ=0 NormalX=0 NormalY=0 NormalZ=1 AngleXU=0 Radius=0.55
  constraints (5):
    c: Coincident(g0,g-1)
    c: PointOnObject(g0,g-3)
    c: Horizontal(g0)
    c: Coincident(g1,g0)
    c: PointOnObject(g0,g1)
FEATURE [PartDesign::Pocket] Pocket  label="Hinge pin hole"
  BaseFeature = -> AdditiveLoft001
  Direction = (0.224951,0,0.97437)
  Length = 5
  Length2 = 5
  Midplane = true
  Profile = -> Sketch010
  ReferenceAxis = -> Sketch010 [N_Axis]
  Suppressed = false
  Type = 1
FEATURE [PartDesign::Plane] DatumPlane003  label="Hinge inner middle top profile plane"
  AttachmentSupport = -> [Sketch]
  Length = 160.885
  MapMode = 7
  Placement = pos=(0.562378,5e-16,2.43593) rot=(0.704823,-0.704823,-0.080304;2.98133rad)
  ResizeMode = 0
  Width = 84.0412
FEATURE [PartDesign::Plane] DatumPlane004  label="Hinge inner middle bottom profile plane"
  AttachmentSupport = -> [Sketch]
  Length = 160.885
  MapMode = 7
  Placement = pos=(-0.562378,-5e-16,-2.43593) rot=(0.704823,-0.704823,-0.080304;2.98133rad)
  ResizeMode = 0
  Width = 84.0412
FEATURE [Sketcher::SketchObject] Sketch011
  ArcFitTolerance = 1e-06
  AttachmentSupport = -> [DatumPlane003]
  ExternalGeometry = -> [Sketch001]
  ExternalTypes = [0]
  FullyConstrained = true
  MakeInternals = false
  MapMode = 5
  Placement = pos=(0.562378,5e-16,2.43593) rot=(0.704823,-0.704823,-0.080304;2.98133rad)
  sketch-geometry (8):
    g0: ArcOfCircle CenterX=0 CenterY=0 CenterZ=0 NormalX=0 NormalY=0 NormalZ=1 AngleXU=0 Radius=1.65 StartAngle=3.14159 EndAngle=5.23096
    g1: LineSegment [constr] StartX=1.5 StartY=0 StartZ=0 EndX=0 EndY=0 EndZ=0
    g2: LineSegment StartX=-1.65 StartY=2.5 StartZ=0 EndX=7.70983 EndY=2.5 EndZ=0
    g3: LineSegment StartX=-1.65 StartY=0 StartZ=0 EndX=-1.65 EndY=2.5 EndZ=0
    g4: LineSegment [constr] StartX=0.743463 StartY=-1.30279 StartZ=0 EndX=0.81781 EndY=-1.43307 EndZ=0
    g5: Circle [constr] CenterX=0 CenterY=0 CenterZ=0 NormalX=0 NormalY=0 NormalZ=1 AngleXU=0 Radius=1.5
    g6: LineSegment StartX=0.81781 StartY=-1.43307 StartZ=0 EndX=7.70983 EndY=2.5 EndZ=0
    g7: LineSegment [constr] StartX=0 StartY=1.5 StartZ=0 EndX=0 EndY=2.5 EndZ=0
  constraints (23):
    c: Coincident(g0,g-1)
    c: Coincident(g1,g0)
    c: Horizontal(g2)
    c: Coincident(g3,g2)
    c: Vertical(g3)
    c: PointOnObject(g1,g-3)
    c: PointOnObject(g1,g-1)
    c: PointOnObject(g0,g-1)
    c: Coincident(g3,g0)
    c: Coincident(g4,g0)
    c: Coincident(g5,g0)
    c: PointOnObject(g1,g5)
    c: PointOnObject(g4,g5)
    c: Coincident(g6,g2)
    c: Tangent(g6,g0) = -1.5708
    c: Distance(g4,g0) = 0.15
    c: PointOnObject(g7,g5)
    c: PointOnObject(g7,g2)
    c: PointOnObject(g0,g7)
    c: Vertical(g7)
    c: DistanceY(g7,g7) = 1
    c: PointOnObject(g0,g4)
    c: Angle(g-4,g6) = 0.698132
FEATURE [Sketcher::SketchObject] Sketch012
  ArcFitTolerance = 1e-06
  AttachmentSupport = -> [DatumPlane004]
  ExternalGeometry = -> [Sketch011]
  ExternalTypes = [0]
  FullyConstrained = true
  MakeInternals = false
  MapMode = 5
  Placement = pos=(-0.562378,-5e-16,-2.43593) rot=(0.704823,-0.704823,-0.080304;2.98133rad)
  sketch-geometry (4):
    g0: ArcOfCircle CenterX=0 CenterY=0 CenterZ=0 NormalX=0 NormalY=0 NormalZ=1 AngleXU=0 Radius=1.65 StartAngle=3.14159 EndAngle=5.23097
    g1: LineSegment StartX=-1.65 StartY=0 StartZ=0 EndX=-1.65 EndY=2.5 EndZ=0
    g2: LineSegment StartX=-1.65 StartY=2.5 StartZ=0 EndX=7.70983 EndY=2.5 EndZ=0
    g3: LineSegment StartX=7.70983 StartY=2.5 StartZ=0 EndX=0.817826 EndY=-1.43306 EndZ=0
  constraints (9):
    c: Coincident(g0,g-1)
    c: Coincident(g0,g-3)
    c: Coincident(g1,g-3)
    c: Coincident(g1,g-3)
    c: Coincident(g2,g1)
    c: Coincident(g2,g-4)
    c: Coincident(g3,g-4)
    c: Coincident(g3,g0)
    c: PointOnObject(g0,g-4)
FEATURE [PartDesign::SubtractiveLoft] SubtractiveLoft  label="Slot for frame hinge"
  BaseFeature = -> Pocket
  Closed = false
  Profile = -> Sketch011
  Ruled = false
  Sections = -> [Sketch012]
  Suppressed = false
FEATURE [Sketcher::SketchObject] Sketch013  label="Ear hook wire master sketch"
  ArcFitTolerance = 1e-06
  AttachmentSupport = -> [SubtractiveLoft]
  ExternalTypes = [0]
  FullyConstrained = true
  MakeInternals = false
  MapMode = 5
  Placement = pos=(0.449978,0.083825,0) rot=(0.648089,-0.538508,-0.538508;1.99153rad)
  sketch-geometry (10):
    g0: LineSegment StartX=0 StartY=0 StartZ=0 EndX=60 EndY=0.000652174 EndZ=0
    g1: LineSegment StartX=60 StartY=0.000652174 StartZ=0 EndX=70 EndY=0.00076087 EndZ=0
    g2: LineSegment [constr] StartX=95.7998 StartY=-46.4455 StartZ=0 EndX=91.0994 EndY=-23.4871 EndZ=0
    g3: LineSegment StartX=70 StartY=0.00076087 StartZ=0 EndX=92 EndY=0.001 EndZ=0
    g4: LineSegment StartX=95.7998 StartY=-46.4455 StartZ=0 EndX=95.7016 EndY=-46.4642 EndZ=0
    g5: ArcOfEllipse CenterX=91.0994 CenterY=-23.4871 CenterZ=0 NormalX=0 NormalY=0 NormalZ=1 MajorRadius=26.5 MinorRadius=23.4247 AngleXU=0.139637 StartAngle=4.76748 EndAngle=7.69631
    g6: LineSegment [constr] StartX=117.341 StartY=-19.7987 StartZ=0 EndX=64.8573 EndY=-27.1755 EndZ=0
    g7: GeomPoint [constr] X=103.37 Y=-21.7625 Z=0
    g8: GeomPoint [constr] X=78.8291 Y=-25.2117 Z=0
    g9: LineSegment [constr] StartX=117.543 StartY=-22.6869 StartZ=0 EndX=117.543 EndY=-46.4642 EndZ=0
  constraints (27):
    c: Coincident(g-1,g0)
    c: Distance(g0,g0) = 60
    c: Coincident(g1,g0)
    c: Parallel(g0,g1)
    c: Distance(g1,g1) = 10
    c: Coincident(g2,g5)
    c: Parallel(g1,g3)
    c: Distance(g3,g-1) = 0.001
    c: Tangent(g4,g5) = 1.5708
    c: Distance(g4,g4) = 0.1
    c: InternalAlignment(g6,g5)
    c: InternalAlignment(g7,g5)
    c: InternalAlignment(g8,g5)
    c: Coincident(g1,g3)
    c: Coincident(g5,g2)
    c: Distance(g3,g3) = 22
    c: Distance(g2,g6) = 26.5
    c: Distance(g6,g3) = 19.8
    c: Tangent(g3,g5) = 1.5708
    c: Angle(g2,g3) = 1.36886
    c: Angle(g3,g6) = 0.139626
    c: Tangent(g9,g5) = 1.5708
    c: Vertical(g9)
    c: Horizontal(g4,g9)
    c: Distance(g9,g-2) = 117.543
    c: Distance(g2,g-2) = 95.7998
    c: Distance(g2,g-1) = 46.4455
FEATURE [Sketcher::SketchObject] Sketch003
  ArcFitTolerance = 1e-06
  AttachmentSupport = -> [SubtractiveLoft]
  ExternalGeometry = -> [Sketch001,Sketch013,SubtractiveLoft]
  ExternalTypes = [0]
  FullyConstrained = true
  MakeInternals = false
  MapMode = 5
  Placement = pos=(0.449978,0.083825,0) rot=(0.506579,0.609663,0.609663;2.2038rad)
  sketch-geometry (10):
    g0: ArcOfCircle CenterX=-59.9938 CenterY=573.878 CenterZ=0 NormalX=0 NormalY=0 NormalZ=1 AngleXU=0 Radius=571.877 StartAngle=4.71238 EndAngle=4.81485
    g1: LineSegment StartX=-86.9201 StartY=15 StartZ=0 EndX=-86.9201 EndY=-15 EndZ=0
    g2: ArcOfCircle CenterX=-60.0062 CenterY=-573.872 CenterZ=0 NormalX=0 NormalY=0 NormalZ=1 AngleXU=0 Radius=571.873 StartAngle=1.46831 EndAngle=1.57079
    g3: LineSegment StartX=-60 StartY=2.00065 StartZ=0 EndX=-60 EndY=-1.99935 EndZ=0
    g4: LineSegment StartX=-86.9201 StartY=-15 StartZ=0 EndX=3.42249 EndY=-15 EndZ=0
    g5: LineSegment StartX=-1.5 StartY=5 StartZ=0 EndX=3.42249 EndY=5 EndZ=0
    g6: LineSegment StartX=3.42249 StartY=5 StartZ=0 EndX=3.42249 EndY=15 EndZ=0
    g7: LineSegment StartX=-1.5 StartY=-5 StartZ=0 EndX=3.42249 EndY=-5 EndZ=0
    g8: LineSegment StartX=3.42249 StartY=-15 StartZ=0 EndX=3.42249 EndY=-5 EndZ=0
    g9: LineSegment StartX=-86.9201 StartY=15 StartZ=0 EndX=3.42249 EndY=15 EndZ=0
  constraints (28):
    c: Coincident(g4,g1)
    c: Symmetric(g0,g2,g-4)
    c: Symmetric(g9,g4,g-4)
    c: Vertical(g0,g-3)
    c: Coincident(g5,g0)
    c: Coincident(g6,g5)
    c: Coincident(g6,g9)
    c: Horizontal(g5)
    c: Coincident(g7,g2)
    c: Horizontal(g7)
    c: Coincident(g8,g4)
    c: Coincident(g8,g7)
    c: Distance(g5,g7) = 10
    c: PointOnObject(g0,g3)
    c: PointOnObject(g2,g3)
    c: Coincident(g0,g3)
    c: Distance(g3,g3) = 4
    c: Coincident(g3,g2)
    c: Symmetric(g0,g2,g-5)
    c: PointOnObject(g-5,g3)
    c: Vertical(g1)
    c: Horizontal(g4)
    c: Coincident(g1,g9)
    c: Coincident(g1,g-6)
    c: PointOnObject(g-6,g9)
    c: Vertical(g6)
    c: Vertical(g8)
    c: PointOnObject(g-7,g6)
FEATURE [PartDesign::Pocket] Pocket001  label="Temple #1"
  BaseFeature = -> SubtractiveLoft
  Direction = (-0.983087,-0.183137,1e-16)
  Length = 5
  Length2 = 5
  Midplane = true
  Profile = -> Sketch003
  ReferenceAxis = -> Sketch003 [N_Axis]
  Refine = true
  Suppressed = false
  Type = 1
FEATURE [Sketcher::SketchObject] Sketch005
  ArcFitTolerance = 1e-06
  AttachmentSupport = -> [Pocket001]
  ExternalGeometry = -> [Sketch003]
  ExternalTypes = [0]
  FullyConstrained = true
  MakeInternals = false
  MapMode = 5
  Placement = pos=(0.449978,0.083825,0) rot=(0.506579,0.609663,0.609663;2.2038rad)
  sketch-geometry (10):
    g0: LineSegment [constr] StartX=-1.5 StartY=5 StartZ=0 EndX=0 EndY=5.15396 EndZ=0
    g1: LineSegment [constr] StartX=-1.5 StartY=2.98949 StartZ=0 EndX=0 EndY=3.14345 EndZ=0
    g2: LineSegment [constr] StartX=-1.5 StartY=-5 StartZ=0 EndX=0 EndY=-5.15399 EndZ=0
    g3: LineSegment [constr] StartX=-1.5 StartY=-2.98949 StartZ=0 EndX=0 EndY=-3.14348 EndZ=0
    g4: ArcOfCircle CenterX=-59.8938 CenterY=571.922 CenterZ=0 NormalX=0 NormalY=0 NormalZ=1 AngleXU=0 Radius=571.922 StartAngle=4.71238 EndAngle=4.81467
    g5: LineSegment [constr] StartX=-60 StartY=2.00065 StartZ=0 EndX=-60 EndY=0.000652174 EndZ=0
    g6: LineSegment [constr] StartX=-60 StartY=-1.99935 StartZ=0 EndX=-60 EndY=0.000652174 EndZ=0
    g7: LineSegment [constr] StartX=-60 StartY=0.000652174 StartZ=0 EndX=-59.9 EndY=0.000651087 EndZ=0
    g8: ArcOfCircle CenterX=-59.9062 CenterY=-571.917 CenterZ=0 NormalX=0 NormalY=0 NormalZ=1 AngleXU=0 Radius=571.917 StartAngle=1.46849 EndAngle=1.57079
    g9: LineSegment StartX=-1.5 StartY=2.98949 StartZ=0 EndX=-1.5 EndY=-2.98949 EndZ=0
  constraints (27):
    c: PointOnObject(g0,g-2)
    c: PointOnObject(g1,g-2)
    c: Parallel(g1,g0)
    c: Distance(g0,g1) = 2
    c: PointOnObject(g2,g-2)
    c: PointOnObject(g3,g-2)
    c: Parallel(g2,g3)
    c: Distance(g3,g2) = 2
    c: Coincident(g-3,g0)
    c: Coincident(g-4,g2)
    c: Coincident(g5,g-3)
    c: Coincident(g6,g-4)
    c: Coincident(g6,g5)
    c: Coincident(g7,g5)
    c: Parallel(g6,g5)
    c: Distance(g7,g7) = 0.1
    c: Equal(g5,g6)
    c: Perpendicular(g5,g7)
    c: Tangent(g7,g4) = -1.5708
    c: Coincident(g4,g8)
    c: Tangent(g8,g7)
    c: Tangent(g4,g1) = -1.5708
    c: Tangent(g8,g3) = 1.5708
    c: Vertical(g1,g0)
    c: Vertical(g3,g2)
    c: Coincident(g9,g1)
    c: Coincident(g9,g3)
FEATURE [PartDesign::Pocket] Pocket002  label="Temple #2"
  BaseFeature = -> Pocket001
  Direction = (-0.983087,-0.183137,1e-16)
  Length = 5
  Length2 = 5
  Midplane = true
  Profile = -> Sketch005
  ReferenceAxis = -> Sketch005 [N_Axis]
  Refine = true
  Suppressed = false
  Type = 1
FEATURE [PartDesign::Plane] DatumPlane  label="Ear hook wire root plane"
  AttachmentOffset = pos=(0,0,10) rot=(0,0,1;0rad)
  AttachmentSupport = -> [Pocket002,Sketch013]
  Length = 86.4693
  MapMode = 6
  Placement = pos=(13.2695,-68.7323,0.00076087) rot=(0.60966,-0.506577,0.609667;2.20379rad)
  ResizeMode = 0
  Width = 89.7919
FEATURE [Sketcher::SketchObject] Sketch006  label="Ear hook wire root profile"
  ArcFitTolerance = 1e-06
  AttachmentSupport = -> [DatumPlane]
  ExternalGeometry = -> [Pocket002]
  ExternalTypes = [0]
  FullyConstrained = true
  MakeInternals = false
  MapMode = 5
  Placement = pos=(13.2695,-68.7323,0.00076087) rot=(0.60966,-0.506577,0.609667;2.20379rad)
  sketch-geometry (4):
    g0: LineSegment StartX=-1 StartY=-2 StartZ=0 EndX=1 EndY=-2 EndZ=0
    g1: ArcOfCircle CenterX=-1 CenterY=-1 CenterZ=0 NormalX=0 NormalY=0 NormalZ=1 AngleXU=0 Radius=1 StartAngle=1.5708 EndAngle=4.71239
    g2: ArcOfCircle CenterX=1 CenterY=-1 CenterZ=0 NormalX=0 NormalY=0 NormalZ=1 AngleXU=0 Radius=1 StartAngle=4.71239 EndAngle=7.85398
    g3: LineSegment StartX=-1 StartY=2.14e-14 StartZ=0 EndX=1 EndY=2.14e-14 EndZ=0
  constraints (13):
    c: PointOnObject(g0,g-3)
    c: Symmetric(g0,g0,g-2)
    c: Coincident(g1,g0)
    c: Vertical(g1,g0)
    c: Vertical(g1,g1)
    c: Coincident(g2,g0)
    c: Vertical(g0,g2)
    c: Horizontal(g1,g2)
    c: Vertical(g2,g2)
    c: Coincident(g3,g1)
    c: Coincident(g3,g2)
    c: Distance(g3,g0) = 2
    c: Tangent(g1,g-4)
FEATURE [PartDesign::AdditiveLoft] AdditiveLoft  label="Temple-to-ear-hook transition"
  BaseFeature = -> Pocket002
  Closed = false
  Profile = -> Pocket002 [Face3]
  Refine = true
  Ruled = false
  Sections = -> [Sketch006]
  Suppressed = false
FEATURE [Sketcher::SketchObject] Sketch014  label="Ear hook wire center"
  ArcFitTolerance = 1e-06
  AttachmentSupport = -> [DatumPlane]
  ExternalGeometry = -> [Sketch006]
  ExternalTypes = [0]
  FullyConstrained = true
  MakeInternals = false
  MapMode = 5
  Placement = pos=(13.2695,-68.7323,0.00076087) rot=(0.60966,-0.506577,0.609667;2.20379rad)
  sketch-geometry (2):
    g0: LineSegment StartX=-1 StartY=2.49e-14 StartZ=0 EndX=-2e-16 EndY=-1 EndZ=0
    g1: LineSegment StartX=-2e-16 StartY=-1 StartZ=0 EndX=1 EndY=-2 EndZ=0
  constraints (5):
    c: Coincident(g0,g-4)
    c: Coincident(g1,g0)
    c: Coincident(g1,g-3)
    c: Equal(g0,g1)
    c: Parallel(g0,g1)
FEATURE [PartDesign::Plane] DatumPlane006  label="Ear hook wire center plane"
  AttachmentSupport = -> [Sketch014,AdditiveLoft]
  Length = 169.117
  MapMode = 6
  Placement = pos=(14.2526,-68.5492,0.00076087) rot=(0.648089,-0.538508,-0.538508;1.99153rad)
  ResizeMode = 0
  Width = 92.4295
FEATURE [Sketcher::SketchObject] Sketch015  label="Ear hook wire path"
  ArcFitTolerance = 1e-06
  AttachmentSupport = -> [DatumPlane006]
  ExternalGeometry = -> [Sketch013]
  ExternalTypes = [0]
  FullyConstrained = true
  MakeInternals = false
  MapMode = 5
  Placement = pos=(14.2526,-68.5492,0.00076087) rot=(0.648089,-0.538508,-0.538508;1.99153rad)
  sketch-geometry (7):
    g0: ArcOfEllipse CenterX=21.0994 CenterY=-23.4879 CenterZ=0 NormalX=0 NormalY=0 NormalZ=1 MajorRadius=26.5 MinorRadius=23.4247 AngleXU=-0.0383248 StartAngle=4.92567 EndAngle=7.85398
    g1: LineSegment [constr] StartX=47.5799 StartY=-24.5032 StartZ=0 EndX=-5.38116 EndY=-22.4725 EndZ=0
    g2: LineSegment [constr] StartX=21.9969 StartY=-0.0803619 StartZ=0 EndX=20.2019 EndY=-46.8954 EndZ=0
    g3: GeomPoint [constr] X=33.4811 Y=-23.9626 Z=0
    g4: GeomPoint [constr] X=8.71761 Y=-23.0131 Z=0
    g5: LineSegment [constr] StartX=21.0994 StartY=-23.4879 StartZ=0 EndX=25.7998 EndY=-46.4463 EndZ=0
    g6: LineSegment StartX=21.9969 StartY=-0.0803619 StartZ=0 EndX=0 EndY=0 EndZ=0
  constraints (10):
    c: InternalAlignment(g1-g4 -> g0) x4
    c: Coincident(g0,g-4)
    c: Equal(g-4,g0)
    c: PointOnObject(g-3,g2)
    c: Coincident(g5,g0)
    c: Coincident(g5,g-5)
    c: PointOnObject(g0,g5)
    c: PointOnObject(g0,g2)
    c: Coincident(g6,g0)
    c: Coincident(g6,g-1)
FEATURE [PartDesign::Plane] DatumPlane007  label="Ear hook wire end plane"
  AttachmentSupport = -> [Sketch015]
  Length = 91.8465
  MapMode = 7
  Placement = pos=(18.9825,-93.9395,-46.5792) rot=(-0.069864,0.756518,0.65023;3.26154rad)
  ResizeMode = 0
  Width = 110.016
FEATURE [Sketcher::SketchObject] Sketch016  label="Ear hook wire end profile"
  ArcFitTolerance = 1e-06
  AttachmentSupport = -> [DatumPlane007]
  ExternalTypes = [0]
  FullyConstrained = true
  MakeInternals = false
  MapMode = 5
  Placement = pos=(18.9825,-93.9395,-46.5792) rot=(-0.069864,0.756518,0.65023;3.26154rad)
  sketch-geometry (4):
    g0: ArcOfCircle CenterX=0 CenterY=0.05 CenterZ=0 NormalX=0 NormalY=0 NormalZ=1 AngleXU=0 Radius=1 StartAngle=0 EndAngle=3.14159
    g1: ArcOfCircle CenterX=0 CenterY=-0.05 CenterZ=0 NormalX=0 NormalY=0 NormalZ=1 AngleXU=0 Radius=1 StartAngle=3.14159 EndAngle=6.28319
    g2: LineSegment StartX=-1 StartY=0.05 StartZ=0 EndX=-1 EndY=-0.05 EndZ=0
    g3: LineSegment StartX=1 StartY=0.05 StartZ=0 EndX=1 EndY=-0.05 EndZ=0
  constraints (13):
    c: Horizontal(g0,g0)
    c: Horizontal(g0,g0)
    c: Horizontal(g1,g1)
    c: Horizontal(g1,g1)
    c: Symmetric(g1,g0,g-1)
    c: Coincident(g2,g0)
    c: Coincident(g2,g1)
    c: Vertical(g2)
    c: Coincident(g0,g3)
    c: Coincident(g1,g3)
    c: Distance(g3,g2) = 2
    c: DistanceY(g2,g2) = 0.1
    c: PointOnObject(g0,g-2)
FEATURE [PartDesign::AdditivePipe] AdditivePipe  label="Ear hook wire"
  AuxilleryCurvelinear = true
  AuxillerySpineTangent = false
  BaseFeature = -> AdditiveLoft
  Binormal = (0,0,0)
  Mode = 0
  Profile = -> Sketch006
  Refine = true
  Sections = -> [Sketch016]
  Spine = -> Sketch015
  SpineTangent = false
  Suppressed = false
  Transformation = 1
  Transition = 0
FEATURE [PartDesign::Fillet] Fillet  label="Ear hook wire end"
  Base = -> AdditivePipe [Edge109]
  BaseFeature = -> AdditivePipe
  Radius = 0.95
  Refine = true
  SupportTransform = false
  Suppressed = false
  UseAllEdges = false
FEATURE [PartDesign::Body] Body
  AllowCompound = false
  Group = -> [Sketch001,Sketch003,Pad,Sketch,DatumPlane001,DatumPlane002,DatumLine,DatumLine001,DatumLine002,Sketch008,Sketch009,AdditiveLoft001,Sketch010,Pocket,DatumPlane003,DatumPlane004,Sketch011,Sketch012,SubtractiveLoft,Sketch013,Pocket001,Sketch005,Pocket002,DatumPlane,Sketch006,AdditiveLoft,Sketch014,DatumPlane006,Sketch015,DatumPlane007,Sketch016,AdditivePipe,Fillet]
  Origin = -> Origin001
  Tip = -> Fillet
FEATURE [App::Part] Part  label="Right temple"
  Group = -> [Body]
  Origin = -> Origin
FEATURE [App::Point] Origin002  label="Origin"
  Role = Origin
FEATURE [App::Point] Origin003  label="Origin"
  Role = Origin
